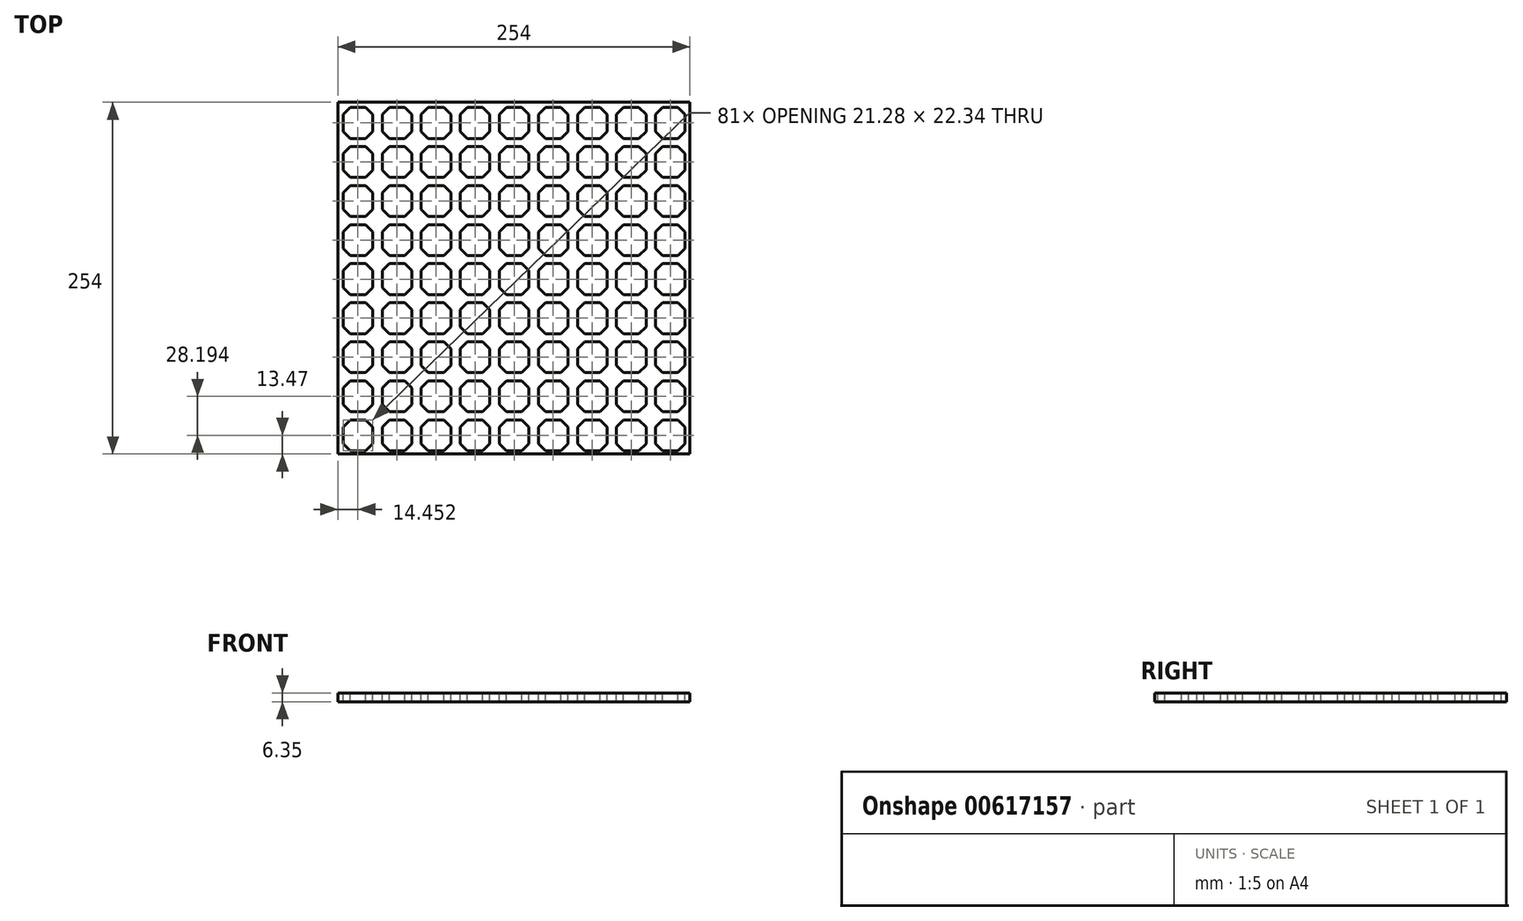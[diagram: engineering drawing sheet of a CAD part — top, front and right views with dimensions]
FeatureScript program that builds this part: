
annotation { "Feature Type Name" : "Feature", "Feature Type Description" : "" }
export const myFeature = defineFeature(function(context is Context, id is Id, definition is map)
    precondition{}
    {
        {
            var Q0;
            Q0=qCreatedBy(makeId("Top.planeOp"),FACE);
            var sketch = newSketch(context, id + "F0", { "sketchPlane" : qUnion([Q0])});
            skLineSegment(sketch, "E0.bottom", {"start": v(-127, 127) * mm, "end": v(127, 127) * mm});
            skLineSegment(sketch, "E0.top", {"start": v(-127, -127) * mm, "end": v(127, -127) * mm});
            skLineSegment(sketch, "E0.left", {"start": v(-127, 127) * mm, "end": v(-127, -127) * mm});
            skLineSegment(sketch, "E0.right", {"start": v(127, 127) * mm, "end": v(127, -127) * mm});
            skSolve(sketch);
        }
        {
            var Q0;
            Q0 = qSketchRegion(id + "F0", true);
            extrude(context, id + "F1", {"entities" : qUnion([Q0]), "depth" : 6.35 * mm, "offsetDistance" : 25.4 * mm});
        }
        {
            var Q0;
            Q0=makeQuery(id+"F1.opExtrude","CAP_FACE",FACE,{"disambiguationData":[OSD([sQuery(id+"F0.wireOp",EDGE,"E0.bottom"),sQuery(id+"F0.wireOp",EDGE,"E0.top"),sQuery(id+"F0.wireOp",EDGE,"E0.left"),sQuery(id+"F0.wireOp",EDGE,"E0.right")])],"isStart":false});
            var sketch = newSketch(context, id + "F2", { "sketchPlane" : qUnion([Q0])});
            skLineSegment(sketch, "E1.bottom", {"start": v(-118.11, 123.2) * mm, "end": v(-106.99, 123.2) * mm});
            skLineSegment(sketch, "E1.top", {"start": v(-118.11, 100.85) * mm, "end": v(-106.99, 100.85) * mm});
            skLineSegment(sketch, "E1.left", {"start": v(-123.2, 118.11) * mm, "end": v(-123.2, 105.93) * mm});
            skLineSegment(sketch, "E1.right", {"start": v(-101.9, 118.11) * mm, "end": v(-101.9, 105.93) * mm});
            skLineSegment(sketch, "E2", {"start": v(-123.2, 118.11) * mm, "end": v(-118.11, 123.2) * mm});
            skPoint(sketch, "E3.orphan", {"position": v(-123.2, 123.2) * mm});
            skLineSegment(sketch, "E4", {"start": v(-106.99, 123.2) * mm, "end": v(-101.9, 118.11) * mm});
            skLineSegment(sketch, "E5", {"start": v(-123.2, 105.93) * mm, "end": v(-118.11, 100.85) * mm});
            skLineSegment(sketch, "E6", {"start": v(-101.9, 105.93) * mm, "end": v(-106.99, 100.85) * mm});
            skPoint(sketch, "E7.orphan", {"position": v(-101.9, 123.2) * mm});
            skPoint(sketch, "E8.orphan", {"position": v(-101.9, 100.85) * mm});
            skPoint(sketch, "E9.orphan", {"position": v(-123.2, 100.85) * mm});
            skLineSegment(sketch, "E10.1.0.0", {"start": v(-73.71, 118.11) * mm, "end": v(-73.71, 105.93) * mm});
            skLineSegment(sketch, "E10.1.0.1", {"start": v(-95, 118.11) * mm, "end": v(-95, 105.93) * mm});
            skLineSegment(sketch, "E10.1.0.2", {"start": v(-89.92, 100.85) * mm, "end": v(-78.8, 100.85) * mm});
            skLineSegment(sketch, "E10.1.0.3", {"start": v(-89.92, 123.2) * mm, "end": v(-78.8, 123.2) * mm});
            skPoint(sketch, "E10.1.0.4", {"position": v(-95, 123.2) * mm});
            skPoint(sketch, "E10.1.0.5", {"position": v(-73.71, 100.85) * mm});
            skPoint(sketch, "E10.1.0.6", {"position": v(-73.71, 123.2) * mm});
            skPoint(sketch, "E10.1.0.7", {"position": v(-95, 100.85) * mm});
            skLineSegment(sketch, "E10.1.0.8", {"start": v(-95, 118.11) * mm, "end": v(-89.92, 123.2) * mm});
            skLineSegment(sketch, "E10.1.0.9", {"start": v(-95, 105.93) * mm, "end": v(-89.92, 100.85) * mm});
            skLineSegment(sketch, "E10.1.0.10", {"start": v(-78.8, 123.2) * mm, "end": v(-73.71, 118.11) * mm});
            skLineSegment(sketch, "E10.1.0.11", {"start": v(-73.71, 105.93) * mm, "end": v(-78.8, 100.85) * mm});
            skLineSegment(sketch, "E10.2.0.0", {"start": v(-45.52, 118.11) * mm, "end": v(-45.52, 105.93) * mm});
            skLineSegment(sketch, "E10.2.0.1", {"start": v(-66.8, 118.11) * mm, "end": v(-66.8, 105.93) * mm});
            skLineSegment(sketch, "E10.2.0.2", {"start": v(-61.72, 100.85) * mm, "end": v(-50.6, 100.85) * mm});
            skLineSegment(sketch, "E10.2.0.3", {"start": v(-61.72, 123.2) * mm, "end": v(-50.6, 123.2) * mm});
            skPoint(sketch, "E10.2.0.4", {"position": v(-66.8, 123.2) * mm});
            skPoint(sketch, "E10.2.0.5", {"position": v(-45.52, 100.85) * mm});
            skPoint(sketch, "E10.2.0.6", {"position": v(-45.52, 123.2) * mm});
            skPoint(sketch, "E10.2.0.7", {"position": v(-66.8, 100.85) * mm});
            skLineSegment(sketch, "E10.2.0.8", {"start": v(-66.8, 118.11) * mm, "end": v(-61.72, 123.2) * mm});
            skLineSegment(sketch, "E10.2.0.9", {"start": v(-66.8, 105.93) * mm, "end": v(-61.72, 100.85) * mm});
            skLineSegment(sketch, "E10.2.0.10", {"start": v(-50.6, 123.2) * mm, "end": v(-45.52, 118.11) * mm});
            skLineSegment(sketch, "E10.2.0.11", {"start": v(-45.52, 105.93) * mm, "end": v(-50.6, 100.85) * mm});
            skLineSegment(sketch, "E10.3.0.0", {"start": v(-17.32, 118.11) * mm, "end": v(-17.32, 105.93) * mm});
            skLineSegment(sketch, "E10.3.0.1", {"start": v(-38.6, 118.11) * mm, "end": v(-38.6, 105.93) * mm});
            skLineSegment(sketch, "E10.3.0.2", {"start": v(-33.53, 100.85) * mm, "end": v(-22.4, 100.85) * mm});
            skLineSegment(sketch, "E10.3.0.3", {"start": v(-33.53, 123.2) * mm, "end": v(-22.4, 123.2) * mm});
            skPoint(sketch, "E10.3.0.4", {"position": v(-38.6, 123.2) * mm});
            skPoint(sketch, "E10.3.0.5", {"position": v(-17.32, 100.85) * mm});
            skPoint(sketch, "E10.3.0.6", {"position": v(-17.32, 123.2) * mm});
            skPoint(sketch, "E10.3.0.7", {"position": v(-38.6, 100.85) * mm});
            skLineSegment(sketch, "E10.3.0.8", {"start": v(-38.6, 118.11) * mm, "end": v(-33.53, 123.2) * mm});
            skLineSegment(sketch, "E10.3.0.9", {"start": v(-38.6, 105.93) * mm, "end": v(-33.53, 100.85) * mm});
            skLineSegment(sketch, "E10.3.0.10", {"start": v(-22.4, 123.2) * mm, "end": v(-17.32, 118.11) * mm});
            skLineSegment(sketch, "E10.3.0.11", {"start": v(-17.32, 105.93) * mm, "end": v(-22.4, 100.85) * mm});
            skLineSegment(sketch, "E10.4.0.0", {"start": v(10.87, 118.11) * mm, "end": v(10.87, 105.93) * mm});
            skLineSegment(sketch, "E10.4.0.1", {"start": v(-10.41, 118.11) * mm, "end": v(-10.41, 105.93) * mm});
            skLineSegment(sketch, "E10.4.0.2", {"start": v(-5.33, 100.85) * mm, "end": v(5.79, 100.85) * mm});
            skLineSegment(sketch, "E10.4.0.3", {"start": v(-5.33, 123.2) * mm, "end": v(5.79, 123.2) * mm});
            skPoint(sketch, "E10.4.0.4", {"position": v(-10.41, 123.2) * mm});
            skPoint(sketch, "E10.4.0.5", {"position": v(10.87, 100.85) * mm});
            skPoint(sketch, "E10.4.0.6", {"position": v(10.87, 123.2) * mm});
            skPoint(sketch, "E10.4.0.7", {"position": v(-10.41, 100.85) * mm});
            skLineSegment(sketch, "E10.4.0.8", {"start": v(-10.41, 118.11) * mm, "end": v(-5.33, 123.2) * mm});
            skLineSegment(sketch, "E10.4.0.9", {"start": v(-10.41, 105.93) * mm, "end": v(-5.33, 100.85) * mm});
            skLineSegment(sketch, "E10.4.0.10", {"start": v(5.79, 123.2) * mm, "end": v(10.87, 118.11) * mm});
            skLineSegment(sketch, "E10.4.0.11", {"start": v(10.87, 105.93) * mm, "end": v(5.79, 100.85) * mm});
            skLineSegment(sketch, "E10.5.0.0", {"start": v(39.06, 118.11) * mm, "end": v(39.06, 105.93) * mm});
            skLineSegment(sketch, "E10.5.0.1", {"start": v(17.78, 118.11) * mm, "end": v(17.78, 105.93) * mm});
            skLineSegment(sketch, "E10.5.0.2", {"start": v(22.86, 100.85) * mm, "end": v(33.98, 100.85) * mm});
            skLineSegment(sketch, "E10.5.0.3", {"start": v(22.86, 123.2) * mm, "end": v(33.98, 123.2) * mm});
            skPoint(sketch, "E10.5.0.4", {"position": v(17.78, 123.2) * mm});
            skPoint(sketch, "E10.5.0.5", {"position": v(39.06, 100.85) * mm});
            skPoint(sketch, "E10.5.0.6", {"position": v(39.06, 123.2) * mm});
            skPoint(sketch, "E10.5.0.7", {"position": v(17.78, 100.85) * mm});
            skLineSegment(sketch, "E10.5.0.8", {"start": v(17.78, 118.11) * mm, "end": v(22.86, 123.2) * mm});
            skLineSegment(sketch, "E10.5.0.9", {"start": v(17.78, 105.93) * mm, "end": v(22.86, 100.85) * mm});
            skLineSegment(sketch, "E10.5.0.10", {"start": v(33.98, 123.2) * mm, "end": v(39.06, 118.11) * mm});
            skLineSegment(sketch, "E10.5.0.11", {"start": v(39.06, 105.93) * mm, "end": v(33.98, 100.85) * mm});
            skLineSegment(sketch, "E10.6.0.0", {"start": v(67.26, 118.11) * mm, "end": v(67.26, 105.93) * mm});
            skLineSegment(sketch, "E10.6.0.1", {"start": v(45.97, 118.11) * mm, "end": v(45.97, 105.93) * mm});
            skLineSegment(sketch, "E10.6.0.2", {"start": v(51.05, 100.85) * mm, "end": v(62.18, 100.85) * mm});
            skLineSegment(sketch, "E10.6.0.3", {"start": v(51.05, 123.2) * mm, "end": v(62.18, 123.2) * mm});
            skPoint(sketch, "E10.6.0.4", {"position": v(45.97, 123.2) * mm});
            skPoint(sketch, "E10.6.0.5", {"position": v(67.26, 100.85) * mm});
            skPoint(sketch, "E10.6.0.6", {"position": v(67.26, 123.2) * mm});
            skPoint(sketch, "E10.6.0.7", {"position": v(45.97, 100.85) * mm});
            skLineSegment(sketch, "E10.6.0.8", {"start": v(45.97, 118.11) * mm, "end": v(51.05, 123.2) * mm});
            skLineSegment(sketch, "E10.6.0.9", {"start": v(45.97, 105.93) * mm, "end": v(51.05, 100.85) * mm});
            skLineSegment(sketch, "E10.6.0.10", {"start": v(62.18, 123.2) * mm, "end": v(67.26, 118.11) * mm});
            skLineSegment(sketch, "E10.6.0.11", {"start": v(67.26, 105.93) * mm, "end": v(62.18, 100.85) * mm});
            skLineSegment(sketch, "E10.7.0.0", {"start": v(95.45, 118.11) * mm, "end": v(95.45, 105.93) * mm});
            skLineSegment(sketch, "E10.7.0.1", {"start": v(74.17, 118.11) * mm, "end": v(74.17, 105.93) * mm});
            skLineSegment(sketch, "E10.7.0.2", {"start": v(79.25, 100.85) * mm, "end": v(90.37, 100.85) * mm});
            skLineSegment(sketch, "E10.7.0.3", {"start": v(79.25, 123.2) * mm, "end": v(90.37, 123.2) * mm});
            skPoint(sketch, "E10.7.0.4", {"position": v(74.17, 123.2) * mm});
            skPoint(sketch, "E10.7.0.5", {"position": v(95.45, 100.85) * mm});
            skPoint(sketch, "E10.7.0.6", {"position": v(95.45, 123.2) * mm});
            skPoint(sketch, "E10.7.0.7", {"position": v(74.17, 100.85) * mm});
            skLineSegment(sketch, "E10.7.0.8", {"start": v(74.17, 118.11) * mm, "end": v(79.25, 123.2) * mm});
            skLineSegment(sketch, "E10.7.0.9", {"start": v(74.17, 105.93) * mm, "end": v(79.25, 100.85) * mm});
            skLineSegment(sketch, "E10.7.0.10", {"start": v(90.37, 123.2) * mm, "end": v(95.45, 118.11) * mm});
            skLineSegment(sketch, "E10.7.0.11", {"start": v(95.45, 105.93) * mm, "end": v(90.37, 100.85) * mm});
            skLineSegment(sketch, "E10.8.0.0", {"start": v(123.65, 118.11) * mm, "end": v(123.65, 105.93) * mm});
            skLineSegment(sketch, "E10.8.0.1", {"start": v(102.36, 118.11) * mm, "end": v(102.36, 105.93) * mm});
            skLineSegment(sketch, "E10.8.0.2", {"start": v(107.44, 100.85) * mm, "end": v(118.57, 100.85) * mm});
            skLineSegment(sketch, "E10.8.0.3", {"start": v(107.44, 123.2) * mm, "end": v(118.57, 123.2) * mm});
            skPoint(sketch, "E10.8.0.4", {"position": v(102.36, 123.2) * mm});
            skPoint(sketch, "E10.8.0.5", {"position": v(123.65, 100.85) * mm});
            skPoint(sketch, "E10.8.0.6", {"position": v(123.65, 123.2) * mm});
            skPoint(sketch, "E10.8.0.7", {"position": v(102.36, 100.85) * mm});
            skLineSegment(sketch, "E10.8.0.8", {"start": v(102.36, 118.11) * mm, "end": v(107.44, 123.2) * mm});
            skLineSegment(sketch, "E10.8.0.9", {"start": v(102.36, 105.93) * mm, "end": v(107.44, 100.85) * mm});
            skLineSegment(sketch, "E10.8.0.10", {"start": v(118.57, 123.2) * mm, "end": v(123.65, 118.11) * mm});
            skLineSegment(sketch, "E10.8.0.11", {"start": v(123.65, 105.93) * mm, "end": v(118.57, 100.85) * mm});
            skLineSegment(sketch, "E10.9.0.0", {"start": v(151.84, 118.11) * mm, "end": v(151.84, 105.93) * mm});
            skLineSegment(sketch, "E10.9.0.1", {"start": v(130.56, 118.11) * mm, "end": v(130.56, 105.93) * mm});
            skLineSegment(sketch, "E10.9.0.2", {"start": v(135.64, 100.85) * mm, "end": v(146.76, 100.85) * mm});
            skLineSegment(sketch, "E10.9.0.3", {"start": v(135.64, 123.2) * mm, "end": v(146.76, 123.2) * mm});
            skPoint(sketch, "E10.9.0.4", {"position": v(130.56, 123.2) * mm});
            skPoint(sketch, "E10.9.0.5", {"position": v(151.84, 100.85) * mm});
            skPoint(sketch, "E10.9.0.6", {"position": v(151.84, 123.2) * mm});
            skPoint(sketch, "E10.9.0.7", {"position": v(130.56, 100.85) * mm});
            skLineSegment(sketch, "E10.9.0.8", {"start": v(130.56, 118.11) * mm, "end": v(135.64, 123.2) * mm});
            skLineSegment(sketch, "E10.9.0.9", {"start": v(130.56, 105.93) * mm, "end": v(135.64, 100.85) * mm});
            skLineSegment(sketch, "E10.9.0.10", {"start": v(146.76, 123.2) * mm, "end": v(151.84, 118.11) * mm});
            skLineSegment(sketch, "E10.9.0.11", {"start": v(151.84, 105.93) * mm, "end": v(146.76, 100.85) * mm});
            skLineSegment(sketch, "E10.direction1", {"start": v(-123.2, 100.85) * mm, "end": v(-95, 100.85) * mm, "construction": true});
            skPoint(sketch, "E11.0.1.0", {"position": v(-73.71, 95) * mm});
            skLineSegment(sketch, "E11.0.1.1", {"start": v(102.36, 89.92) * mm, "end": v(102.36, 77.74) * mm});
            skLineSegment(sketch, "E11.0.1.2", {"start": v(45.97, 89.92) * mm, "end": v(45.97, 77.74) * mm});
            skPoint(sketch, "E11.0.1.3", {"position": v(39.06, 95) * mm});
            skLineSegment(sketch, "E11.0.1.4", {"start": v(-66.8, 89.92) * mm, "end": v(-66.8, 77.74) * mm});
            skLineSegment(sketch, "E11.0.1.5", {"start": v(-95, 89.92) * mm, "end": v(-95, 77.74) * mm});
            skLineSegment(sketch, "E11.0.1.6", {"start": v(-73.71, 89.92) * mm, "end": v(-73.71, 77.74) * mm});
            skLineSegment(sketch, "E11.0.1.7", {"start": v(-123.2, 89.92) * mm, "end": v(-123.2, 77.74) * mm});
            skLineSegment(sketch, "E11.0.1.8", {"start": v(-101.9, 89.92) * mm, "end": v(-101.9, 77.74) * mm});
            skPoint(sketch, "E11.0.1.9", {"position": v(130.56, 72.66) * mm});
            skPoint(sketch, "E11.0.1.10", {"position": v(67.26, 95) * mm});
            skPoint(sketch, "E11.0.1.11", {"position": v(-66.8, 72.66) * mm});
            skPoint(sketch, "E11.0.1.12", {"position": v(10.87, 95) * mm});
            skPoint(sketch, "E11.0.1.13", {"position": v(-101.9, 72.66) * mm});
            skPoint(sketch, "E11.0.1.14", {"position": v(45.97, 72.66) * mm});
            skLineSegment(sketch, "E11.0.1.15", {"start": v(-118.11, 95) * mm, "end": v(-106.99, 95) * mm});
            skPoint(sketch, "E11.0.1.16", {"position": v(-45.52, 95) * mm});
            skPoint(sketch, "E11.0.1.17", {"position": v(151.84, 95) * mm});
            skPoint(sketch, "E11.0.1.18", {"position": v(123.65, 95) * mm});
            skLineSegment(sketch, "E11.0.1.19", {"start": v(151.84, 89.92) * mm, "end": v(151.84, 77.74) * mm});
            skLineSegment(sketch, "E11.0.1.20", {"start": v(95.45, 89.92) * mm, "end": v(95.45, 77.74) * mm});
            skLineSegment(sketch, "E11.0.1.21", {"start": v(39.06, 89.92) * mm, "end": v(39.06, 77.74) * mm});
            skLineSegment(sketch, "E11.0.1.22", {"start": v(-17.32, 89.92) * mm, "end": v(-17.32, 77.74) * mm});
            skPoint(sketch, "E11.0.1.23", {"position": v(74.17, 72.66) * mm});
            skPoint(sketch, "E11.0.1.24", {"position": v(-38.6, 72.66) * mm});
            skLineSegment(sketch, "E11.0.1.25", {"start": v(-10.41, 89.92) * mm, "end": v(-10.41, 77.74) * mm});
            skLineSegment(sketch, "E11.0.1.26", {"start": v(-89.92, 72.66) * mm, "end": v(-78.8, 72.66) * mm});
            skLineSegment(sketch, "E11.0.1.27", {"start": v(-45.52, 89.92) * mm, "end": v(-45.52, 77.74) * mm});
            skLineSegment(sketch, "E11.0.1.28", {"start": v(10.87, 89.92) * mm, "end": v(10.87, 77.74) * mm});
            skPoint(sketch, "E11.0.1.29", {"position": v(-17.32, 95) * mm});
            skPoint(sketch, "E11.0.1.30", {"position": v(95.45, 95) * mm});
            skPoint(sketch, "E11.0.1.31", {"position": v(95.45, 72.66) * mm});
            skPoint(sketch, "E11.0.1.32", {"position": v(151.84, 72.66) * mm});
            skPoint(sketch, "E11.0.1.33", {"position": v(-73.71, 72.66) * mm});
            skPoint(sketch, "E11.0.1.34", {"position": v(39.06, 72.66) * mm});
            skLineSegment(sketch, "E11.0.1.35", {"start": v(67.26, 89.92) * mm, "end": v(67.26, 77.74) * mm});
            skLineSegment(sketch, "E11.0.1.36", {"start": v(123.65, 89.92) * mm, "end": v(123.65, 77.74) * mm});
            skLineSegment(sketch, "E11.0.1.37", {"start": v(-123.2, 72.66) * mm, "end": v(-95, 72.66) * mm, "construction": true});
            skPoint(sketch, "E11.0.1.38", {"position": v(130.56, 95) * mm});
            skPoint(sketch, "E11.0.1.39", {"position": v(45.97, 95) * mm});
            skLineSegment(sketch, "E11.0.1.40", {"start": v(51.05, 95) * mm, "end": v(62.18, 95) * mm});
            skPoint(sketch, "E11.0.1.41", {"position": v(-66.8, 95) * mm});
            skLineSegment(sketch, "E11.0.1.42", {"start": v(107.44, 95) * mm, "end": v(118.57, 95) * mm});
            skLineSegment(sketch, "E11.0.1.43", {"start": v(135.64, 95) * mm, "end": v(146.76, 95) * mm});
            skLineSegment(sketch, "E11.0.1.44", {"start": v(79.25, 95) * mm, "end": v(90.37, 95) * mm});
            skLineSegment(sketch, "E11.0.1.45", {"start": v(22.86, 95) * mm, "end": v(33.98, 95) * mm});
            skLineSegment(sketch, "E11.0.1.46", {"start": v(-33.53, 95) * mm, "end": v(-22.4, 95) * mm});
            skLineSegment(sketch, "E11.0.1.47", {"start": v(-61.72, 95) * mm, "end": v(-50.6, 95) * mm});
            skPoint(sketch, "E11.0.1.48", {"position": v(-17.32, 72.66) * mm});
            skLineSegment(sketch, "E11.0.1.49", {"start": v(-5.33, 95) * mm, "end": v(5.79, 95) * mm});
            skLineSegment(sketch, "E11.0.1.50", {"start": v(-33.53, 72.66) * mm, "end": v(-22.4, 72.66) * mm});
            skLineSegment(sketch, "E11.0.1.51", {"start": v(22.86, 72.66) * mm, "end": v(33.98, 72.66) * mm});
            skPoint(sketch, "E11.0.1.52", {"position": v(17.78, 95) * mm});
            skLineSegment(sketch, "E11.0.1.53", {"start": v(79.25, 72.66) * mm, "end": v(90.37, 72.66) * mm});
            skLineSegment(sketch, "E11.0.1.54", {"start": v(135.64, 72.66) * mm, "end": v(146.76, 72.66) * mm});
            skPoint(sketch, "E11.0.1.55", {"position": v(67.26, 72.66) * mm});
            skPoint(sketch, "E11.0.1.56", {"position": v(-101.9, 95) * mm});
            skPoint(sketch, "E11.0.1.57", {"position": v(10.87, 72.66) * mm});
            skPoint(sketch, "E11.0.1.58", {"position": v(123.65, 72.66) * mm});
            skPoint(sketch, "E11.0.1.59", {"position": v(-45.52, 72.66) * mm});
            skPoint(sketch, "E11.0.1.60", {"position": v(-95, 72.66) * mm});
            skLineSegment(sketch, "E11.0.1.61", {"start": v(51.05, 72.66) * mm, "end": v(62.18, 72.66) * mm});
            skPoint(sketch, "E11.0.1.62", {"position": v(17.78, 72.66) * mm});
            skLineSegment(sketch, "E11.0.1.63", {"start": v(107.44, 72.66) * mm, "end": v(118.57, 72.66) * mm});
            skLineSegment(sketch, "E11.0.1.64", {"start": v(-61.72, 72.66) * mm, "end": v(-50.6, 72.66) * mm});
            skLineSegment(sketch, "E11.0.1.65", {"start": v(-5.33, 72.66) * mm, "end": v(5.79, 72.66) * mm});
            skPoint(sketch, "E11.0.1.66", {"position": v(-123.2, 95) * mm});
            skPoint(sketch, "E11.0.1.67", {"position": v(-10.41, 95) * mm});
            skPoint(sketch, "E11.0.1.68", {"position": v(102.36, 95) * mm});
            skPoint(sketch, "E11.0.1.69", {"position": v(74.17, 95) * mm});
            skPoint(sketch, "E11.0.1.70", {"position": v(-10.41, 72.66) * mm});
            skPoint(sketch, "E11.0.1.71", {"position": v(102.36, 72.66) * mm});
            skPoint(sketch, "E11.0.1.72", {"position": v(-38.6, 95) * mm});
            skPoint(sketch, "E11.0.1.73", {"position": v(-123.2, 72.66) * mm});
            skPoint(sketch, "E11.0.1.74", {"position": v(-95, 95) * mm});
            skLineSegment(sketch, "E11.0.1.75", {"start": v(-38.6, 89.92) * mm, "end": v(-38.6, 77.74) * mm});
            skLineSegment(sketch, "E11.0.1.76", {"start": v(17.78, 89.92) * mm, "end": v(17.78, 77.74) * mm});
            skLineSegment(sketch, "E11.0.1.77", {"start": v(74.17, 89.92) * mm, "end": v(74.17, 77.74) * mm});
            skLineSegment(sketch, "E11.0.1.78", {"start": v(130.56, 89.92) * mm, "end": v(130.56, 77.74) * mm});
            skLineSegment(sketch, "E11.0.1.79", {"start": v(-118.11, 72.66) * mm, "end": v(-106.99, 72.66) * mm});
            skLineSegment(sketch, "E11.0.1.80", {"start": v(-89.92, 95) * mm, "end": v(-78.8, 95) * mm});
            skLineSegment(sketch, "E11.0.1.81", {"start": v(-78.8, 95) * mm, "end": v(-73.71, 89.92) * mm});
            skLineSegment(sketch, "E11.0.1.82", {"start": v(-95, 77.74) * mm, "end": v(-89.92, 72.66) * mm});
            skLineSegment(sketch, "E11.0.1.83", {"start": v(33.98, 95) * mm, "end": v(39.06, 89.92) * mm});
            skLineSegment(sketch, "E11.0.1.84", {"start": v(-73.71, 77.74) * mm, "end": v(-78.8, 72.66) * mm});
            skLineSegment(sketch, "E11.0.1.85", {"start": v(-123.2, 89.92) * mm, "end": v(-118.11, 95) * mm});
            skLineSegment(sketch, "E11.0.1.86", {"start": v(-106.99, 95) * mm, "end": v(-101.9, 89.92) * mm});
            skLineSegment(sketch, "E11.0.1.87", {"start": v(-123.2, 77.74) * mm, "end": v(-118.11, 72.66) * mm});
            skLineSegment(sketch, "E11.0.1.88", {"start": v(-101.9, 77.74) * mm, "end": v(-106.99, 72.66) * mm});
            skLineSegment(sketch, "E11.0.1.89", {"start": v(-45.52, 77.74) * mm, "end": v(-50.6, 72.66) * mm});
            skLineSegment(sketch, "E11.0.1.90", {"start": v(10.87, 77.74) * mm, "end": v(5.79, 72.66) * mm});
            skLineSegment(sketch, "E11.0.1.91", {"start": v(67.26, 77.74) * mm, "end": v(62.18, 72.66) * mm});
            skLineSegment(sketch, "E11.0.1.92", {"start": v(123.65, 77.74) * mm, "end": v(118.57, 72.66) * mm});
            skLineSegment(sketch, "E11.0.1.93", {"start": v(62.18, 95) * mm, "end": v(67.26, 89.92) * mm});
            skLineSegment(sketch, "E11.0.1.94", {"start": v(39.06, 77.74) * mm, "end": v(33.98, 72.66) * mm});
            skLineSegment(sketch, "E11.0.1.95", {"start": v(118.57, 95) * mm, "end": v(123.65, 89.92) * mm});
            skLineSegment(sketch, "E11.0.1.96", {"start": v(95.45, 77.74) * mm, "end": v(90.37, 72.66) * mm});
            skLineSegment(sketch, "E11.0.1.97", {"start": v(151.84, 77.74) * mm, "end": v(146.76, 72.66) * mm});
            skLineSegment(sketch, "E11.0.1.98", {"start": v(-50.6, 95) * mm, "end": v(-45.52, 89.92) * mm});
            skLineSegment(sketch, "E11.0.1.99", {"start": v(5.79, 95) * mm, "end": v(10.87, 89.92) * mm});
            skLineSegment(sketch, "E11.0.1.100", {"start": v(-17.32, 77.74) * mm, "end": v(-22.4, 72.66) * mm});
            skLineSegment(sketch, "E11.0.1.101", {"start": v(-38.6, 77.74) * mm, "end": v(-33.53, 72.66) * mm});
            skLineSegment(sketch, "E11.0.1.102", {"start": v(-10.41, 89.92) * mm, "end": v(-5.33, 95) * mm});
            skLineSegment(sketch, "E11.0.1.103", {"start": v(-66.8, 89.92) * mm, "end": v(-61.72, 95) * mm});
            skLineSegment(sketch, "E11.0.1.104", {"start": v(130.56, 77.74) * mm, "end": v(135.64, 72.66) * mm});
            skLineSegment(sketch, "E11.0.1.105", {"start": v(102.36, 89.92) * mm, "end": v(107.44, 95) * mm});
            skLineSegment(sketch, "E11.0.1.106", {"start": v(74.17, 77.74) * mm, "end": v(79.25, 72.66) * mm});
            skLineSegment(sketch, "E11.0.1.107", {"start": v(45.97, 89.92) * mm, "end": v(51.05, 95) * mm});
            skLineSegment(sketch, "E11.0.1.108", {"start": v(17.78, 77.74) * mm, "end": v(22.86, 72.66) * mm});
            skLineSegment(sketch, "E11.0.1.109", {"start": v(130.56, 89.92) * mm, "end": v(135.64, 95) * mm});
            skLineSegment(sketch, "E11.0.1.110", {"start": v(74.17, 89.92) * mm, "end": v(79.25, 95) * mm});
            skLineSegment(sketch, "E11.0.1.111", {"start": v(17.78, 89.92) * mm, "end": v(22.86, 95) * mm});
            skLineSegment(sketch, "E11.0.1.112", {"start": v(-95, 89.92) * mm, "end": v(-89.92, 95) * mm});
            skLineSegment(sketch, "E11.0.1.113", {"start": v(-38.6, 89.92) * mm, "end": v(-33.53, 95) * mm});
            skLineSegment(sketch, "E11.0.1.114", {"start": v(-22.4, 95) * mm, "end": v(-17.32, 89.92) * mm});
            skLineSegment(sketch, "E11.0.1.115", {"start": v(-10.41, 77.74) * mm, "end": v(-5.33, 72.66) * mm});
            skLineSegment(sketch, "E11.0.1.116", {"start": v(-66.8, 77.74) * mm, "end": v(-61.72, 72.66) * mm});
            skLineSegment(sketch, "E11.0.1.117", {"start": v(146.76, 95) * mm, "end": v(151.84, 89.92) * mm});
            skLineSegment(sketch, "E11.0.1.118", {"start": v(102.36, 77.74) * mm, "end": v(107.44, 72.66) * mm});
            skLineSegment(sketch, "E11.0.1.119", {"start": v(90.37, 95) * mm, "end": v(95.45, 89.92) * mm});
            skLineSegment(sketch, "E11.0.1.120", {"start": v(45.97, 77.74) * mm, "end": v(51.05, 72.66) * mm});
            skPoint(sketch, "E11.0.2.0", {"position": v(-73.71, 66.8) * mm});
            skLineSegment(sketch, "E11.0.2.1", {"start": v(102.36, 61.72) * mm, "end": v(102.36, 49.55) * mm});
            skLineSegment(sketch, "E11.0.2.2", {"start": v(45.97, 61.72) * mm, "end": v(45.97, 49.55) * mm});
            skPoint(sketch, "E11.0.2.3", {"position": v(39.06, 66.8) * mm});
            skLineSegment(sketch, "E11.0.2.4", {"start": v(-66.8, 61.72) * mm, "end": v(-66.8, 49.55) * mm});
            skLineSegment(sketch, "E11.0.2.5", {"start": v(-95, 61.72) * mm, "end": v(-95, 49.55) * mm});
            skLineSegment(sketch, "E11.0.2.6", {"start": v(-73.71, 61.72) * mm, "end": v(-73.71, 49.55) * mm});
            skLineSegment(sketch, "E11.0.2.7", {"start": v(-123.2, 61.72) * mm, "end": v(-123.2, 49.55) * mm});
            skLineSegment(sketch, "E11.0.2.8", {"start": v(-101.9, 61.72) * mm, "end": v(-101.9, 49.55) * mm});
            skPoint(sketch, "E11.0.2.9", {"position": v(130.56, 44.47) * mm});
            skPoint(sketch, "E11.0.2.10", {"position": v(67.26, 66.8) * mm});
            skPoint(sketch, "E11.0.2.11", {"position": v(-66.8, 44.47) * mm});
            skPoint(sketch, "E11.0.2.12", {"position": v(10.87, 66.8) * mm});
            skPoint(sketch, "E11.0.2.13", {"position": v(-101.9, 44.47) * mm});
            skPoint(sketch, "E11.0.2.14", {"position": v(45.97, 44.47) * mm});
            skLineSegment(sketch, "E11.0.2.15", {"start": v(-118.11, 66.8) * mm, "end": v(-106.99, 66.8) * mm});
            skPoint(sketch, "E11.0.2.16", {"position": v(-45.52, 66.8) * mm});
            skPoint(sketch, "E11.0.2.17", {"position": v(151.84, 66.8) * mm});
            skPoint(sketch, "E11.0.2.18", {"position": v(123.65, 66.8) * mm});
            skLineSegment(sketch, "E11.0.2.19", {"start": v(151.84, 61.72) * mm, "end": v(151.84, 49.55) * mm});
            skLineSegment(sketch, "E11.0.2.20", {"start": v(95.45, 61.72) * mm, "end": v(95.45, 49.55) * mm});
            skLineSegment(sketch, "E11.0.2.21", {"start": v(39.06, 61.72) * mm, "end": v(39.06, 49.55) * mm});
            skLineSegment(sketch, "E11.0.2.22", {"start": v(-17.32, 61.72) * mm, "end": v(-17.32, 49.55) * mm});
            skPoint(sketch, "E11.0.2.23", {"position": v(74.17, 44.47) * mm});
            skPoint(sketch, "E11.0.2.24", {"position": v(-38.6, 44.47) * mm});
            skLineSegment(sketch, "E11.0.2.25", {"start": v(-10.41, 61.72) * mm, "end": v(-10.41, 49.55) * mm});
            skLineSegment(sketch, "E11.0.2.26", {"start": v(-89.92, 44.47) * mm, "end": v(-78.8, 44.47) * mm});
            skLineSegment(sketch, "E11.0.2.27", {"start": v(-45.52, 61.72) * mm, "end": v(-45.52, 49.55) * mm});
            skLineSegment(sketch, "E11.0.2.28", {"start": v(10.87, 61.72) * mm, "end": v(10.87, 49.55) * mm});
            skPoint(sketch, "E11.0.2.29", {"position": v(-17.32, 66.8) * mm});
            skPoint(sketch, "E11.0.2.30", {"position": v(95.45, 66.8) * mm});
            skPoint(sketch, "E11.0.2.31", {"position": v(95.45, 44.47) * mm});
            skPoint(sketch, "E11.0.2.32", {"position": v(151.84, 44.47) * mm});
            skPoint(sketch, "E11.0.2.33", {"position": v(-73.71, 44.47) * mm});
            skPoint(sketch, "E11.0.2.34", {"position": v(39.06, 44.47) * mm});
            skLineSegment(sketch, "E11.0.2.35", {"start": v(67.26, 61.72) * mm, "end": v(67.26, 49.55) * mm});
            skLineSegment(sketch, "E11.0.2.36", {"start": v(123.65, 61.72) * mm, "end": v(123.65, 49.55) * mm});
            skLineSegment(sketch, "E11.0.2.37", {"start": v(-123.2, 44.47) * mm, "end": v(-95, 44.47) * mm, "construction": true});
            skPoint(sketch, "E11.0.2.38", {"position": v(130.56, 66.8) * mm});
            skPoint(sketch, "E11.0.2.39", {"position": v(45.97, 66.8) * mm});
            skLineSegment(sketch, "E11.0.2.40", {"start": v(51.05, 66.8) * mm, "end": v(62.18, 66.8) * mm});
            skPoint(sketch, "E11.0.2.41", {"position": v(-66.8, 66.8) * mm});
            skLineSegment(sketch, "E11.0.2.42", {"start": v(107.44, 66.8) * mm, "end": v(118.57, 66.8) * mm});
            skLineSegment(sketch, "E11.0.2.43", {"start": v(135.64, 66.8) * mm, "end": v(146.76, 66.8) * mm});
            skLineSegment(sketch, "E11.0.2.44", {"start": v(79.25, 66.8) * mm, "end": v(90.37, 66.8) * mm});
            skLineSegment(sketch, "E11.0.2.45", {"start": v(22.86, 66.8) * mm, "end": v(33.98, 66.8) * mm});
            skLineSegment(sketch, "E11.0.2.46", {"start": v(-33.53, 66.8) * mm, "end": v(-22.4, 66.8) * mm});
            skLineSegment(sketch, "E11.0.2.47", {"start": v(-61.72, 66.8) * mm, "end": v(-50.6, 66.8) * mm});
            skPoint(sketch, "E11.0.2.48", {"position": v(-17.32, 44.47) * mm});
            skLineSegment(sketch, "E11.0.2.49", {"start": v(-5.33, 66.8) * mm, "end": v(5.79, 66.8) * mm});
            skLineSegment(sketch, "E11.0.2.50", {"start": v(-33.53, 44.47) * mm, "end": v(-22.4, 44.47) * mm});
            skLineSegment(sketch, "E11.0.2.51", {"start": v(22.86, 44.47) * mm, "end": v(33.98, 44.47) * mm});
            skPoint(sketch, "E11.0.2.52", {"position": v(17.78, 66.8) * mm});
            skLineSegment(sketch, "E11.0.2.53", {"start": v(79.25, 44.47) * mm, "end": v(90.37, 44.47) * mm});
            skLineSegment(sketch, "E11.0.2.54", {"start": v(135.64, 44.47) * mm, "end": v(146.76, 44.47) * mm});
            skPoint(sketch, "E11.0.2.55", {"position": v(67.26, 44.47) * mm});
            skPoint(sketch, "E11.0.2.56", {"position": v(-101.9, 66.8) * mm});
            skPoint(sketch, "E11.0.2.57", {"position": v(10.87, 44.47) * mm});
            skPoint(sketch, "E11.0.2.58", {"position": v(123.65, 44.47) * mm});
            skPoint(sketch, "E11.0.2.59", {"position": v(-45.52, 44.47) * mm});
            skPoint(sketch, "E11.0.2.60", {"position": v(-95, 44.47) * mm});
            skLineSegment(sketch, "E11.0.2.61", {"start": v(51.05, 44.47) * mm, "end": v(62.18, 44.47) * mm});
            skPoint(sketch, "E11.0.2.62", {"position": v(17.78, 44.47) * mm});
            skLineSegment(sketch, "E11.0.2.63", {"start": v(107.44, 44.47) * mm, "end": v(118.57, 44.47) * mm});
            skLineSegment(sketch, "E11.0.2.64", {"start": v(-61.72, 44.47) * mm, "end": v(-50.6, 44.47) * mm});
            skLineSegment(sketch, "E11.0.2.65", {"start": v(-5.33, 44.47) * mm, "end": v(5.79, 44.47) * mm});
            skPoint(sketch, "E11.0.2.66", {"position": v(-123.2, 66.8) * mm});
            skPoint(sketch, "E11.0.2.67", {"position": v(-10.41, 66.8) * mm});
            skPoint(sketch, "E11.0.2.68", {"position": v(102.36, 66.8) * mm});
            skPoint(sketch, "E11.0.2.69", {"position": v(74.17, 66.8) * mm});
            skPoint(sketch, "E11.0.2.70", {"position": v(-10.41, 44.47) * mm});
            skPoint(sketch, "E11.0.2.71", {"position": v(102.36, 44.47) * mm});
            skPoint(sketch, "E11.0.2.72", {"position": v(-38.6, 66.8) * mm});
            skPoint(sketch, "E11.0.2.73", {"position": v(-123.2, 44.47) * mm});
            skPoint(sketch, "E11.0.2.74", {"position": v(-95, 66.8) * mm});
            skLineSegment(sketch, "E11.0.2.75", {"start": v(-38.6, 61.72) * mm, "end": v(-38.6, 49.55) * mm});
            skLineSegment(sketch, "E11.0.2.76", {"start": v(17.78, 61.72) * mm, "end": v(17.78, 49.55) * mm});
            skLineSegment(sketch, "E11.0.2.77", {"start": v(74.17, 61.72) * mm, "end": v(74.17, 49.55) * mm});
            skLineSegment(sketch, "E11.0.2.78", {"start": v(130.56, 61.72) * mm, "end": v(130.56, 49.55) * mm});
            skLineSegment(sketch, "E11.0.2.79", {"start": v(-118.11, 44.47) * mm, "end": v(-106.99, 44.47) * mm});
            skLineSegment(sketch, "E11.0.2.80", {"start": v(-89.92, 66.8) * mm, "end": v(-78.8, 66.8) * mm});
            skLineSegment(sketch, "E11.0.2.81", {"start": v(-78.8, 66.8) * mm, "end": v(-73.71, 61.72) * mm});
            skLineSegment(sketch, "E11.0.2.82", {"start": v(-95, 49.55) * mm, "end": v(-89.92, 44.47) * mm});
            skLineSegment(sketch, "E11.0.2.83", {"start": v(33.98, 66.8) * mm, "end": v(39.06, 61.72) * mm});
            skLineSegment(sketch, "E11.0.2.84", {"start": v(-73.71, 49.55) * mm, "end": v(-78.8, 44.47) * mm});
            skLineSegment(sketch, "E11.0.2.85", {"start": v(-123.2, 61.72) * mm, "end": v(-118.11, 66.8) * mm});
            skLineSegment(sketch, "E11.0.2.86", {"start": v(-106.99, 66.8) * mm, "end": v(-101.9, 61.72) * mm});
            skLineSegment(sketch, "E11.0.2.87", {"start": v(-123.2, 49.55) * mm, "end": v(-118.11, 44.47) * mm});
            skLineSegment(sketch, "E11.0.2.88", {"start": v(-101.9, 49.55) * mm, "end": v(-106.99, 44.47) * mm});
            skLineSegment(sketch, "E11.0.2.89", {"start": v(-45.52, 49.55) * mm, "end": v(-50.6, 44.47) * mm});
            skLineSegment(sketch, "E11.0.2.90", {"start": v(10.87, 49.55) * mm, "end": v(5.79, 44.47) * mm});
            skLineSegment(sketch, "E11.0.2.91", {"start": v(67.26, 49.55) * mm, "end": v(62.18, 44.47) * mm});
            skLineSegment(sketch, "E11.0.2.92", {"start": v(123.65, 49.55) * mm, "end": v(118.57, 44.47) * mm});
            skLineSegment(sketch, "E11.0.2.93", {"start": v(62.18, 66.8) * mm, "end": v(67.26, 61.72) * mm});
            skLineSegment(sketch, "E11.0.2.94", {"start": v(39.06, 49.55) * mm, "end": v(33.98, 44.47) * mm});
            skLineSegment(sketch, "E11.0.2.95", {"start": v(118.57, 66.8) * mm, "end": v(123.65, 61.72) * mm});
            skLineSegment(sketch, "E11.0.2.96", {"start": v(95.45, 49.55) * mm, "end": v(90.37, 44.47) * mm});
            skLineSegment(sketch, "E11.0.2.97", {"start": v(151.84, 49.55) * mm, "end": v(146.76, 44.47) * mm});
            skLineSegment(sketch, "E11.0.2.98", {"start": v(-50.6, 66.8) * mm, "end": v(-45.52, 61.72) * mm});
            skLineSegment(sketch, "E11.0.2.99", {"start": v(5.79, 66.8) * mm, "end": v(10.87, 61.72) * mm});
            skLineSegment(sketch, "E11.0.2.100", {"start": v(-17.32, 49.55) * mm, "end": v(-22.4, 44.47) * mm});
            skLineSegment(sketch, "E11.0.2.101", {"start": v(-38.6, 49.55) * mm, "end": v(-33.53, 44.47) * mm});
            skLineSegment(sketch, "E11.0.2.102", {"start": v(-10.41, 61.72) * mm, "end": v(-5.33, 66.8) * mm});
            skLineSegment(sketch, "E11.0.2.103", {"start": v(-66.8, 61.72) * mm, "end": v(-61.72, 66.8) * mm});
            skLineSegment(sketch, "E11.0.2.104", {"start": v(130.56, 49.55) * mm, "end": v(135.64, 44.47) * mm});
            skLineSegment(sketch, "E11.0.2.105", {"start": v(102.36, 61.72) * mm, "end": v(107.44, 66.8) * mm});
            skLineSegment(sketch, "E11.0.2.106", {"start": v(74.17, 49.55) * mm, "end": v(79.25, 44.47) * mm});
            skLineSegment(sketch, "E11.0.2.107", {"start": v(45.97, 61.72) * mm, "end": v(51.05, 66.8) * mm});
            skLineSegment(sketch, "E11.0.2.108", {"start": v(17.78, 49.55) * mm, "end": v(22.86, 44.47) * mm});
            skLineSegment(sketch, "E11.0.2.109", {"start": v(130.56, 61.72) * mm, "end": v(135.64, 66.8) * mm});
            skLineSegment(sketch, "E11.0.2.110", {"start": v(74.17, 61.72) * mm, "end": v(79.25, 66.8) * mm});
            skLineSegment(sketch, "E11.0.2.111", {"start": v(17.78, 61.72) * mm, "end": v(22.86, 66.8) * mm});
            skLineSegment(sketch, "E11.0.2.112", {"start": v(-95, 61.72) * mm, "end": v(-89.92, 66.8) * mm});
            skLineSegment(sketch, "E11.0.2.113", {"start": v(-38.6, 61.72) * mm, "end": v(-33.53, 66.8) * mm});
            skLineSegment(sketch, "E11.0.2.114", {"start": v(-22.4, 66.8) * mm, "end": v(-17.32, 61.72) * mm});
            skLineSegment(sketch, "E11.0.2.115", {"start": v(-10.41, 49.55) * mm, "end": v(-5.33, 44.47) * mm});
            skLineSegment(sketch, "E11.0.2.116", {"start": v(-66.8, 49.55) * mm, "end": v(-61.72, 44.47) * mm});
            skLineSegment(sketch, "E11.0.2.117", {"start": v(146.76, 66.8) * mm, "end": v(151.84, 61.72) * mm});
            skLineSegment(sketch, "E11.0.2.118", {"start": v(102.36, 49.55) * mm, "end": v(107.44, 44.47) * mm});
            skLineSegment(sketch, "E11.0.2.119", {"start": v(90.37, 66.8) * mm, "end": v(95.45, 61.72) * mm});
            skLineSegment(sketch, "E11.0.2.120", {"start": v(45.97, 49.55) * mm, "end": v(51.05, 44.47) * mm});
            skPoint(sketch, "E11.0.3.0", {"position": v(-73.71, 38.6) * mm});
            skLineSegment(sketch, "E11.0.3.1", {"start": v(102.36, 33.53) * mm, "end": v(102.36, 21.35) * mm});
            skLineSegment(sketch, "E11.0.3.2", {"start": v(45.97, 33.53) * mm, "end": v(45.97, 21.35) * mm});
            skPoint(sketch, "E11.0.3.3", {"position": v(39.06, 38.6) * mm});
            skLineSegment(sketch, "E11.0.3.4", {"start": v(-66.8, 33.53) * mm, "end": v(-66.8, 21.35) * mm});
            skLineSegment(sketch, "E11.0.3.5", {"start": v(-95, 33.53) * mm, "end": v(-95, 21.35) * mm});
            skLineSegment(sketch, "E11.0.3.6", {"start": v(-73.71, 33.53) * mm, "end": v(-73.71, 21.35) * mm});
            skLineSegment(sketch, "E11.0.3.7", {"start": v(-123.2, 33.53) * mm, "end": v(-123.2, 21.35) * mm});
            skLineSegment(sketch, "E11.0.3.8", {"start": v(-101.9, 33.53) * mm, "end": v(-101.9, 21.35) * mm});
            skPoint(sketch, "E11.0.3.9", {"position": v(130.56, 16.27) * mm});
            skPoint(sketch, "E11.0.3.10", {"position": v(67.26, 38.6) * mm});
            skPoint(sketch, "E11.0.3.11", {"position": v(-66.8, 16.27) * mm});
            skPoint(sketch, "E11.0.3.12", {"position": v(10.87, 38.6) * mm});
            skPoint(sketch, "E11.0.3.13", {"position": v(-101.9, 16.27) * mm});
            skPoint(sketch, "E11.0.3.14", {"position": v(45.97, 16.27) * mm});
            skLineSegment(sketch, "E11.0.3.15", {"start": v(-118.11, 38.6) * mm, "end": v(-106.99, 38.6) * mm});
            skPoint(sketch, "E11.0.3.16", {"position": v(-45.52, 38.6) * mm});
            skPoint(sketch, "E11.0.3.17", {"position": v(151.84, 38.6) * mm});
            skPoint(sketch, "E11.0.3.18", {"position": v(123.65, 38.6) * mm});
            skLineSegment(sketch, "E11.0.3.19", {"start": v(151.84, 33.53) * mm, "end": v(151.84, 21.35) * mm});
            skLineSegment(sketch, "E11.0.3.20", {"start": v(95.45, 33.53) * mm, "end": v(95.45, 21.35) * mm});
            skLineSegment(sketch, "E11.0.3.21", {"start": v(39.06, 33.53) * mm, "end": v(39.06, 21.35) * mm});
            skLineSegment(sketch, "E11.0.3.22", {"start": v(-17.32, 33.53) * mm, "end": v(-17.32, 21.35) * mm});
            skPoint(sketch, "E11.0.3.23", {"position": v(74.17, 16.27) * mm});
            skPoint(sketch, "E11.0.3.24", {"position": v(-38.6, 16.27) * mm});
            skLineSegment(sketch, "E11.0.3.25", {"start": v(-10.41, 33.53) * mm, "end": v(-10.41, 21.35) * mm});
            skLineSegment(sketch, "E11.0.3.26", {"start": v(-89.92, 16.27) * mm, "end": v(-78.8, 16.27) * mm});
            skLineSegment(sketch, "E11.0.3.27", {"start": v(-45.52, 33.53) * mm, "end": v(-45.52, 21.35) * mm});
            skLineSegment(sketch, "E11.0.3.28", {"start": v(10.87, 33.53) * mm, "end": v(10.87, 21.35) * mm});
            skPoint(sketch, "E11.0.3.29", {"position": v(-17.32, 38.6) * mm});
            skPoint(sketch, "E11.0.3.30", {"position": v(95.45, 38.6) * mm});
            skPoint(sketch, "E11.0.3.31", {"position": v(95.45, 16.27) * mm});
            skPoint(sketch, "E11.0.3.32", {"position": v(151.84, 16.27) * mm});
            skPoint(sketch, "E11.0.3.33", {"position": v(-73.71, 16.27) * mm});
            skPoint(sketch, "E11.0.3.34", {"position": v(39.06, 16.27) * mm});
            skLineSegment(sketch, "E11.0.3.35", {"start": v(67.26, 33.53) * mm, "end": v(67.26, 21.35) * mm});
            skLineSegment(sketch, "E11.0.3.36", {"start": v(123.65, 33.53) * mm, "end": v(123.65, 21.35) * mm});
            skLineSegment(sketch, "E11.0.3.37", {"start": v(-123.2, 16.27) * mm, "end": v(-95, 16.27) * mm, "construction": true});
            skPoint(sketch, "E11.0.3.38", {"position": v(130.56, 38.6) * mm});
            skPoint(sketch, "E11.0.3.39", {"position": v(45.97, 38.6) * mm});
            skLineSegment(sketch, "E11.0.3.40", {"start": v(51.05, 38.6) * mm, "end": v(62.18, 38.6) * mm});
            skPoint(sketch, "E11.0.3.41", {"position": v(-66.8, 38.6) * mm});
            skLineSegment(sketch, "E11.0.3.42", {"start": v(107.44, 38.6) * mm, "end": v(118.57, 38.6) * mm});
            skLineSegment(sketch, "E11.0.3.43", {"start": v(135.64, 38.6) * mm, "end": v(146.76, 38.6) * mm});
            skLineSegment(sketch, "E11.0.3.44", {"start": v(79.25, 38.6) * mm, "end": v(90.37, 38.6) * mm});
            skLineSegment(sketch, "E11.0.3.45", {"start": v(22.86, 38.6) * mm, "end": v(33.98, 38.6) * mm});
            skLineSegment(sketch, "E11.0.3.46", {"start": v(-33.53, 38.6) * mm, "end": v(-22.4, 38.6) * mm});
            skLineSegment(sketch, "E11.0.3.47", {"start": v(-61.72, 38.6) * mm, "end": v(-50.6, 38.6) * mm});
            skPoint(sketch, "E11.0.3.48", {"position": v(-17.32, 16.27) * mm});
            skLineSegment(sketch, "E11.0.3.49", {"start": v(-5.33, 38.6) * mm, "end": v(5.79, 38.6) * mm});
            skLineSegment(sketch, "E11.0.3.50", {"start": v(-33.53, 16.27) * mm, "end": v(-22.4, 16.27) * mm});
            skLineSegment(sketch, "E11.0.3.51", {"start": v(22.86, 16.27) * mm, "end": v(33.98, 16.27) * mm});
            skPoint(sketch, "E11.0.3.52", {"position": v(17.78, 38.6) * mm});
            skLineSegment(sketch, "E11.0.3.53", {"start": v(79.25, 16.27) * mm, "end": v(90.37, 16.27) * mm});
            skLineSegment(sketch, "E11.0.3.54", {"start": v(135.64, 16.27) * mm, "end": v(146.76, 16.27) * mm});
            skPoint(sketch, "E11.0.3.55", {"position": v(67.26, 16.27) * mm});
            skPoint(sketch, "E11.0.3.56", {"position": v(-101.9, 38.6) * mm});
            skPoint(sketch, "E11.0.3.57", {"position": v(10.87, 16.27) * mm});
            skPoint(sketch, "E11.0.3.58", {"position": v(123.65, 16.27) * mm});
            skPoint(sketch, "E11.0.3.59", {"position": v(-45.52, 16.27) * mm});
            skPoint(sketch, "E11.0.3.60", {"position": v(-95, 16.27) * mm});
            skLineSegment(sketch, "E11.0.3.61", {"start": v(51.05, 16.27) * mm, "end": v(62.18, 16.27) * mm});
            skPoint(sketch, "E11.0.3.62", {"position": v(17.78, 16.27) * mm});
            skLineSegment(sketch, "E11.0.3.63", {"start": v(107.44, 16.27) * mm, "end": v(118.57, 16.27) * mm});
            skLineSegment(sketch, "E11.0.3.64", {"start": v(-61.72, 16.27) * mm, "end": v(-50.6, 16.27) * mm});
            skLineSegment(sketch, "E11.0.3.65", {"start": v(-5.33, 16.27) * mm, "end": v(5.79, 16.27) * mm});
            skPoint(sketch, "E11.0.3.66", {"position": v(-123.2, 38.6) * mm});
            skPoint(sketch, "E11.0.3.67", {"position": v(-10.41, 38.6) * mm});
            skPoint(sketch, "E11.0.3.68", {"position": v(102.36, 38.6) * mm});
            skPoint(sketch, "E11.0.3.69", {"position": v(74.17, 38.6) * mm});
            skPoint(sketch, "E11.0.3.70", {"position": v(-10.41, 16.27) * mm});
            skPoint(sketch, "E11.0.3.71", {"position": v(102.36, 16.27) * mm});
            skPoint(sketch, "E11.0.3.72", {"position": v(-38.6, 38.6) * mm});
            skPoint(sketch, "E11.0.3.73", {"position": v(-123.2, 16.27) * mm});
            skPoint(sketch, "E11.0.3.74", {"position": v(-95, 38.6) * mm});
            skLineSegment(sketch, "E11.0.3.75", {"start": v(-38.6, 33.53) * mm, "end": v(-38.6, 21.35) * mm});
            skLineSegment(sketch, "E11.0.3.76", {"start": v(17.78, 33.53) * mm, "end": v(17.78, 21.35) * mm});
            skLineSegment(sketch, "E11.0.3.77", {"start": v(74.17, 33.53) * mm, "end": v(74.17, 21.35) * mm});
            skLineSegment(sketch, "E11.0.3.78", {"start": v(130.56, 33.53) * mm, "end": v(130.56, 21.35) * mm});
            skLineSegment(sketch, "E11.0.3.79", {"start": v(-118.11, 16.27) * mm, "end": v(-106.99, 16.27) * mm});
            skLineSegment(sketch, "E11.0.3.80", {"start": v(-89.92, 38.6) * mm, "end": v(-78.8, 38.6) * mm});
            skLineSegment(sketch, "E11.0.3.81", {"start": v(-78.8, 38.6) * mm, "end": v(-73.71, 33.53) * mm});
            skLineSegment(sketch, "E11.0.3.82", {"start": v(-95, 21.35) * mm, "end": v(-89.92, 16.27) * mm});
            skLineSegment(sketch, "E11.0.3.83", {"start": v(33.98, 38.6) * mm, "end": v(39.06, 33.53) * mm});
            skLineSegment(sketch, "E11.0.3.84", {"start": v(-73.71, 21.35) * mm, "end": v(-78.8, 16.27) * mm});
            skLineSegment(sketch, "E11.0.3.85", {"start": v(-123.2, 33.53) * mm, "end": v(-118.11, 38.6) * mm});
            skLineSegment(sketch, "E11.0.3.86", {"start": v(-106.99, 38.6) * mm, "end": v(-101.9, 33.53) * mm});
            skLineSegment(sketch, "E11.0.3.87", {"start": v(-123.2, 21.35) * mm, "end": v(-118.11, 16.27) * mm});
            skLineSegment(sketch, "E11.0.3.88", {"start": v(-101.9, 21.35) * mm, "end": v(-106.99, 16.27) * mm});
            skLineSegment(sketch, "E11.0.3.89", {"start": v(-45.52, 21.35) * mm, "end": v(-50.6, 16.27) * mm});
            skLineSegment(sketch, "E11.0.3.90", {"start": v(10.87, 21.35) * mm, "end": v(5.79, 16.27) * mm});
            skLineSegment(sketch, "E11.0.3.91", {"start": v(67.26, 21.35) * mm, "end": v(62.18, 16.27) * mm});
            skLineSegment(sketch, "E11.0.3.92", {"start": v(123.65, 21.35) * mm, "end": v(118.57, 16.27) * mm});
            skLineSegment(sketch, "E11.0.3.93", {"start": v(62.18, 38.6) * mm, "end": v(67.26, 33.53) * mm});
            skLineSegment(sketch, "E11.0.3.94", {"start": v(39.06, 21.35) * mm, "end": v(33.98, 16.27) * mm});
            skLineSegment(sketch, "E11.0.3.95", {"start": v(118.57, 38.6) * mm, "end": v(123.65, 33.53) * mm});
            skLineSegment(sketch, "E11.0.3.96", {"start": v(95.45, 21.35) * mm, "end": v(90.37, 16.27) * mm});
            skLineSegment(sketch, "E11.0.3.97", {"start": v(151.84, 21.35) * mm, "end": v(146.76, 16.27) * mm});
            skLineSegment(sketch, "E11.0.3.98", {"start": v(-50.6, 38.6) * mm, "end": v(-45.52, 33.53) * mm});
            skLineSegment(sketch, "E11.0.3.99", {"start": v(5.79, 38.6) * mm, "end": v(10.87, 33.53) * mm});
            skLineSegment(sketch, "E11.0.3.100", {"start": v(-17.32, 21.35) * mm, "end": v(-22.4, 16.27) * mm});
            skLineSegment(sketch, "E11.0.3.101", {"start": v(-38.6, 21.35) * mm, "end": v(-33.53, 16.27) * mm});
            skLineSegment(sketch, "E11.0.3.102", {"start": v(-10.41, 33.53) * mm, "end": v(-5.33, 38.6) * mm});
            skLineSegment(sketch, "E11.0.3.103", {"start": v(-66.8, 33.53) * mm, "end": v(-61.72, 38.6) * mm});
            skLineSegment(sketch, "E11.0.3.104", {"start": v(130.56, 21.35) * mm, "end": v(135.64, 16.27) * mm});
            skLineSegment(sketch, "E11.0.3.105", {"start": v(102.36, 33.53) * mm, "end": v(107.44, 38.6) * mm});
            skLineSegment(sketch, "E11.0.3.106", {"start": v(74.17, 21.35) * mm, "end": v(79.25, 16.27) * mm});
            skLineSegment(sketch, "E11.0.3.107", {"start": v(45.97, 33.53) * mm, "end": v(51.05, 38.6) * mm});
            skLineSegment(sketch, "E11.0.3.108", {"start": v(17.78, 21.35) * mm, "end": v(22.86, 16.27) * mm});
            skLineSegment(sketch, "E11.0.3.109", {"start": v(130.56, 33.53) * mm, "end": v(135.64, 38.6) * mm});
            skLineSegment(sketch, "E11.0.3.110", {"start": v(74.17, 33.53) * mm, "end": v(79.25, 38.6) * mm});
            skLineSegment(sketch, "E11.0.3.111", {"start": v(17.78, 33.53) * mm, "end": v(22.86, 38.6) * mm});
            skLineSegment(sketch, "E11.0.3.112", {"start": v(-95, 33.53) * mm, "end": v(-89.92, 38.6) * mm});
            skLineSegment(sketch, "E11.0.3.113", {"start": v(-38.6, 33.53) * mm, "end": v(-33.53, 38.6) * mm});
            skLineSegment(sketch, "E11.0.3.114", {"start": v(-22.4, 38.6) * mm, "end": v(-17.32, 33.53) * mm});
            skLineSegment(sketch, "E11.0.3.115", {"start": v(-10.41, 21.35) * mm, "end": v(-5.33, 16.27) * mm});
            skLineSegment(sketch, "E11.0.3.116", {"start": v(-66.8, 21.35) * mm, "end": v(-61.72, 16.27) * mm});
            skLineSegment(sketch, "E11.0.3.117", {"start": v(146.76, 38.6) * mm, "end": v(151.84, 33.53) * mm});
            skLineSegment(sketch, "E11.0.3.118", {"start": v(102.36, 21.35) * mm, "end": v(107.44, 16.27) * mm});
            skLineSegment(sketch, "E11.0.3.119", {"start": v(90.37, 38.6) * mm, "end": v(95.45, 33.53) * mm});
            skLineSegment(sketch, "E11.0.3.120", {"start": v(45.97, 21.35) * mm, "end": v(51.05, 16.27) * mm});
            skPoint(sketch, "E11.0.4.0", {"position": v(-73.71, 10.41) * mm});
            skLineSegment(sketch, "E11.0.4.1", {"start": v(102.36, 5.33) * mm, "end": v(102.36, -6.84) * mm});
            skLineSegment(sketch, "E11.0.4.2", {"start": v(45.97, 5.33) * mm, "end": v(45.97, -6.84) * mm});
            skPoint(sketch, "E11.0.4.3", {"position": v(39.06, 10.41) * mm});
            skLineSegment(sketch, "E11.0.4.4", {"start": v(-66.8, 5.33) * mm, "end": v(-66.8, -6.84) * mm});
            skLineSegment(sketch, "E11.0.4.5", {"start": v(-95, 5.33) * mm, "end": v(-95, -6.84) * mm});
            skLineSegment(sketch, "E11.0.4.6", {"start": v(-73.71, 5.33) * mm, "end": v(-73.71, -6.84) * mm});
            skLineSegment(sketch, "E11.0.4.7", {"start": v(-123.2, 5.33) * mm, "end": v(-123.2, -6.84) * mm});
            skLineSegment(sketch, "E11.0.4.8", {"start": v(-101.9, 5.33) * mm, "end": v(-101.9, -6.84) * mm});
            skPoint(sketch, "E11.0.4.9", {"position": v(130.56, -11.92) * mm});
            skPoint(sketch, "E11.0.4.10", {"position": v(67.26, 10.41) * mm});
            skPoint(sketch, "E11.0.4.11", {"position": v(-66.8, -11.92) * mm});
            skPoint(sketch, "E11.0.4.12", {"position": v(10.87, 10.41) * mm});
            skPoint(sketch, "E11.0.4.13", {"position": v(-101.9, -11.92) * mm});
            skPoint(sketch, "E11.0.4.14", {"position": v(45.97, -11.92) * mm});
            skLineSegment(sketch, "E11.0.4.15", {"start": v(-118.11, 10.41) * mm, "end": v(-106.99, 10.41) * mm});
            skPoint(sketch, "E11.0.4.16", {"position": v(-45.52, 10.41) * mm});
            skPoint(sketch, "E11.0.4.17", {"position": v(151.84, 10.41) * mm});
            skPoint(sketch, "E11.0.4.18", {"position": v(123.65, 10.41) * mm});
            skLineSegment(sketch, "E11.0.4.19", {"start": v(151.84, 5.33) * mm, "end": v(151.84, -6.84) * mm});
            skLineSegment(sketch, "E11.0.4.20", {"start": v(95.45, 5.33) * mm, "end": v(95.45, -6.84) * mm});
            skLineSegment(sketch, "E11.0.4.21", {"start": v(39.06, 5.33) * mm, "end": v(39.06, -6.84) * mm});
            skLineSegment(sketch, "E11.0.4.22", {"start": v(-17.32, 5.33) * mm, "end": v(-17.32, -6.84) * mm});
            skPoint(sketch, "E11.0.4.23", {"position": v(74.17, -11.92) * mm});
            skPoint(sketch, "E11.0.4.24", {"position": v(-38.6, -11.92) * mm});
            skLineSegment(sketch, "E11.0.4.25", {"start": v(-10.41, 5.33) * mm, "end": v(-10.41, -6.84) * mm});
            skLineSegment(sketch, "E11.0.4.26", {"start": v(-89.92, -11.92) * mm, "end": v(-78.8, -11.92) * mm});
            skLineSegment(sketch, "E11.0.4.27", {"start": v(-45.52, 5.33) * mm, "end": v(-45.52, -6.84) * mm});
            skLineSegment(sketch, "E11.0.4.28", {"start": v(10.87, 5.33) * mm, "end": v(10.87, -6.84) * mm});
            skPoint(sketch, "E11.0.4.29", {"position": v(-17.32, 10.41) * mm});
            skPoint(sketch, "E11.0.4.30", {"position": v(95.45, 10.41) * mm});
            skPoint(sketch, "E11.0.4.31", {"position": v(95.45, -11.92) * mm});
            skPoint(sketch, "E11.0.4.32", {"position": v(151.84, -11.92) * mm});
            skPoint(sketch, "E11.0.4.33", {"position": v(-73.71, -11.92) * mm});
            skPoint(sketch, "E11.0.4.34", {"position": v(39.06, -11.92) * mm});
            skLineSegment(sketch, "E11.0.4.35", {"start": v(67.26, 5.33) * mm, "end": v(67.26, -6.84) * mm});
            skLineSegment(sketch, "E11.0.4.36", {"start": v(123.65, 5.33) * mm, "end": v(123.65, -6.84) * mm});
            skLineSegment(sketch, "E11.0.4.37", {"start": v(-123.2, -11.92) * mm, "end": v(-95, -11.92) * mm, "construction": true});
            skPoint(sketch, "E11.0.4.38", {"position": v(130.56, 10.41) * mm});
            skPoint(sketch, "E11.0.4.39", {"position": v(45.97, 10.41) * mm});
            skLineSegment(sketch, "E11.0.4.40", {"start": v(51.05, 10.41) * mm, "end": v(62.18, 10.41) * mm});
            skPoint(sketch, "E11.0.4.41", {"position": v(-66.8, 10.41) * mm});
            skLineSegment(sketch, "E11.0.4.42", {"start": v(107.44, 10.41) * mm, "end": v(118.57, 10.41) * mm});
            skLineSegment(sketch, "E11.0.4.43", {"start": v(135.64, 10.41) * mm, "end": v(146.76, 10.41) * mm});
            skLineSegment(sketch, "E11.0.4.44", {"start": v(79.25, 10.41) * mm, "end": v(90.37, 10.41) * mm});
            skLineSegment(sketch, "E11.0.4.45", {"start": v(22.86, 10.41) * mm, "end": v(33.98, 10.41) * mm});
            skLineSegment(sketch, "E11.0.4.46", {"start": v(-33.53, 10.41) * mm, "end": v(-22.4, 10.41) * mm});
            skLineSegment(sketch, "E11.0.4.47", {"start": v(-61.72, 10.41) * mm, "end": v(-50.6, 10.41) * mm});
            skPoint(sketch, "E11.0.4.48", {"position": v(-17.32, -11.92) * mm});
            skLineSegment(sketch, "E11.0.4.49", {"start": v(-5.33, 10.41) * mm, "end": v(5.79, 10.41) * mm});
            skLineSegment(sketch, "E11.0.4.50", {"start": v(-33.53, -11.92) * mm, "end": v(-22.4, -11.92) * mm});
            skLineSegment(sketch, "E11.0.4.51", {"start": v(22.86, -11.92) * mm, "end": v(33.98, -11.92) * mm});
            skPoint(sketch, "E11.0.4.52", {"position": v(17.78, 10.41) * mm});
            skLineSegment(sketch, "E11.0.4.53", {"start": v(79.25, -11.92) * mm, "end": v(90.37, -11.92) * mm});
            skLineSegment(sketch, "E11.0.4.54", {"start": v(135.64, -11.92) * mm, "end": v(146.76, -11.92) * mm});
            skPoint(sketch, "E11.0.4.55", {"position": v(67.26, -11.92) * mm});
            skPoint(sketch, "E11.0.4.56", {"position": v(-101.9, 10.41) * mm});
            skPoint(sketch, "E11.0.4.57", {"position": v(10.87, -11.92) * mm});
            skPoint(sketch, "E11.0.4.58", {"position": v(123.65, -11.92) * mm});
            skPoint(sketch, "E11.0.4.59", {"position": v(-45.52, -11.92) * mm});
            skPoint(sketch, "E11.0.4.60", {"position": v(-95, -11.92) * mm});
            skLineSegment(sketch, "E11.0.4.61", {"start": v(51.05, -11.92) * mm, "end": v(62.18, -11.92) * mm});
            skPoint(sketch, "E11.0.4.62", {"position": v(17.78, -11.92) * mm});
            skLineSegment(sketch, "E11.0.4.63", {"start": v(107.44, -11.92) * mm, "end": v(118.57, -11.92) * mm});
            skLineSegment(sketch, "E11.0.4.64", {"start": v(-61.72, -11.92) * mm, "end": v(-50.6, -11.92) * mm});
            skLineSegment(sketch, "E11.0.4.65", {"start": v(-5.33, -11.92) * mm, "end": v(5.79, -11.92) * mm});
            skPoint(sketch, "E11.0.4.66", {"position": v(-123.2, 10.41) * mm});
            skPoint(sketch, "E11.0.4.67", {"position": v(-10.41, 10.41) * mm});
            skPoint(sketch, "E11.0.4.68", {"position": v(102.36, 10.41) * mm});
            skPoint(sketch, "E11.0.4.69", {"position": v(74.17, 10.41) * mm});
            skPoint(sketch, "E11.0.4.70", {"position": v(-10.41, -11.92) * mm});
            skPoint(sketch, "E11.0.4.71", {"position": v(102.36, -11.92) * mm});
            skPoint(sketch, "E11.0.4.72", {"position": v(-38.6, 10.41) * mm});
            skPoint(sketch, "E11.0.4.73", {"position": v(-123.2, -11.92) * mm});
            skPoint(sketch, "E11.0.4.74", {"position": v(-95, 10.41) * mm});
            skLineSegment(sketch, "E11.0.4.75", {"start": v(-38.6, 5.33) * mm, "end": v(-38.6, -6.84) * mm});
            skLineSegment(sketch, "E11.0.4.76", {"start": v(17.78, 5.33) * mm, "end": v(17.78, -6.84) * mm});
            skLineSegment(sketch, "E11.0.4.77", {"start": v(74.17, 5.33) * mm, "end": v(74.17, -6.84) * mm});
            skLineSegment(sketch, "E11.0.4.78", {"start": v(130.56, 5.33) * mm, "end": v(130.56, -6.84) * mm});
            skLineSegment(sketch, "E11.0.4.79", {"start": v(-118.11, -11.92) * mm, "end": v(-106.99, -11.92) * mm});
            skLineSegment(sketch, "E11.0.4.80", {"start": v(-89.92, 10.41) * mm, "end": v(-78.8, 10.41) * mm});
            skLineSegment(sketch, "E11.0.4.81", {"start": v(-78.8, 10.41) * mm, "end": v(-73.71, 5.33) * mm});
            skLineSegment(sketch, "E11.0.4.82", {"start": v(-95, -6.84) * mm, "end": v(-89.92, -11.92) * mm});
            skLineSegment(sketch, "E11.0.4.83", {"start": v(33.98, 10.41) * mm, "end": v(39.06, 5.33) * mm});
            skLineSegment(sketch, "E11.0.4.84", {"start": v(-73.71, -6.84) * mm, "end": v(-78.8, -11.92) * mm});
            skLineSegment(sketch, "E11.0.4.85", {"start": v(-123.2, 5.33) * mm, "end": v(-118.11, 10.41) * mm});
            skLineSegment(sketch, "E11.0.4.86", {"start": v(-106.99, 10.41) * mm, "end": v(-101.9, 5.33) * mm});
            skLineSegment(sketch, "E11.0.4.87", {"start": v(-123.2, -6.84) * mm, "end": v(-118.11, -11.92) * mm});
            skLineSegment(sketch, "E11.0.4.88", {"start": v(-101.9, -6.84) * mm, "end": v(-106.99, -11.92) * mm});
            skLineSegment(sketch, "E11.0.4.89", {"start": v(-45.52, -6.84) * mm, "end": v(-50.6, -11.92) * mm});
            skLineSegment(sketch, "E11.0.4.90", {"start": v(10.87, -6.84) * mm, "end": v(5.79, -11.92) * mm});
            skLineSegment(sketch, "E11.0.4.91", {"start": v(67.26, -6.84) * mm, "end": v(62.18, -11.92) * mm});
            skLineSegment(sketch, "E11.0.4.92", {"start": v(123.65, -6.84) * mm, "end": v(118.57, -11.92) * mm});
            skLineSegment(sketch, "E11.0.4.93", {"start": v(62.18, 10.41) * mm, "end": v(67.26, 5.33) * mm});
            skLineSegment(sketch, "E11.0.4.94", {"start": v(39.06, -6.84) * mm, "end": v(33.98, -11.92) * mm});
            skLineSegment(sketch, "E11.0.4.95", {"start": v(118.57, 10.41) * mm, "end": v(123.65, 5.33) * mm});
            skLineSegment(sketch, "E11.0.4.96", {"start": v(95.45, -6.84) * mm, "end": v(90.37, -11.92) * mm});
            skLineSegment(sketch, "E11.0.4.97", {"start": v(151.84, -6.84) * mm, "end": v(146.76, -11.92) * mm});
            skLineSegment(sketch, "E11.0.4.98", {"start": v(-50.6, 10.41) * mm, "end": v(-45.52, 5.33) * mm});
            skLineSegment(sketch, "E11.0.4.99", {"start": v(5.79, 10.41) * mm, "end": v(10.87, 5.33) * mm});
            skLineSegment(sketch, "E11.0.4.100", {"start": v(-17.32, -6.84) * mm, "end": v(-22.4, -11.92) * mm});
            skLineSegment(sketch, "E11.0.4.101", {"start": v(-38.6, -6.84) * mm, "end": v(-33.53, -11.92) * mm});
            skLineSegment(sketch, "E11.0.4.102", {"start": v(-10.41, 5.33) * mm, "end": v(-5.33, 10.41) * mm});
            skLineSegment(sketch, "E11.0.4.103", {"start": v(-66.8, 5.33) * mm, "end": v(-61.72, 10.41) * mm});
            skLineSegment(sketch, "E11.0.4.104", {"start": v(130.56, -6.84) * mm, "end": v(135.64, -11.92) * mm});
            skLineSegment(sketch, "E11.0.4.105", {"start": v(102.36, 5.33) * mm, "end": v(107.44, 10.41) * mm});
            skLineSegment(sketch, "E11.0.4.106", {"start": v(74.17, -6.84) * mm, "end": v(79.25, -11.92) * mm});
            skLineSegment(sketch, "E11.0.4.107", {"start": v(45.97, 5.33) * mm, "end": v(51.05, 10.41) * mm});
            skLineSegment(sketch, "E11.0.4.108", {"start": v(17.78, -6.84) * mm, "end": v(22.86, -11.92) * mm});
            skLineSegment(sketch, "E11.0.4.109", {"start": v(130.56, 5.33) * mm, "end": v(135.64, 10.41) * mm});
            skLineSegment(sketch, "E11.0.4.110", {"start": v(74.17, 5.33) * mm, "end": v(79.25, 10.41) * mm});
            skLineSegment(sketch, "E11.0.4.111", {"start": v(17.78, 5.33) * mm, "end": v(22.86, 10.41) * mm});
            skLineSegment(sketch, "E11.0.4.112", {"start": v(-95, 5.33) * mm, "end": v(-89.92, 10.41) * mm});
            skLineSegment(sketch, "E11.0.4.113", {"start": v(-38.6, 5.33) * mm, "end": v(-33.53, 10.41) * mm});
            skLineSegment(sketch, "E11.0.4.114", {"start": v(-22.4, 10.41) * mm, "end": v(-17.32, 5.33) * mm});
            skLineSegment(sketch, "E11.0.4.115", {"start": v(-10.41, -6.84) * mm, "end": v(-5.33, -11.92) * mm});
            skLineSegment(sketch, "E11.0.4.116", {"start": v(-66.8, -6.84) * mm, "end": v(-61.72, -11.92) * mm});
            skLineSegment(sketch, "E11.0.4.117", {"start": v(146.76, 10.41) * mm, "end": v(151.84, 5.33) * mm});
            skLineSegment(sketch, "E11.0.4.118", {"start": v(102.36, -6.84) * mm, "end": v(107.44, -11.92) * mm});
            skLineSegment(sketch, "E11.0.4.119", {"start": v(90.37, 10.41) * mm, "end": v(95.45, 5.33) * mm});
            skLineSegment(sketch, "E11.0.4.120", {"start": v(45.97, -6.84) * mm, "end": v(51.05, -11.92) * mm});
            skPoint(sketch, "E11.0.5.0", {"position": v(-73.71, -17.78) * mm});
            skLineSegment(sketch, "E11.0.5.1", {"start": v(102.36, -22.86) * mm, "end": v(102.36, -35.04) * mm});
            skLineSegment(sketch, "E11.0.5.2", {"start": v(45.97, -22.86) * mm, "end": v(45.97, -35.04) * mm});
            skPoint(sketch, "E11.0.5.3", {"position": v(39.06, -17.78) * mm});
            skLineSegment(sketch, "E11.0.5.4", {"start": v(-66.8, -22.86) * mm, "end": v(-66.8, -35.04) * mm});
            skLineSegment(sketch, "E11.0.5.5", {"start": v(-95, -22.86) * mm, "end": v(-95, -35.04) * mm});
            skLineSegment(sketch, "E11.0.5.6", {"start": v(-73.71, -22.86) * mm, "end": v(-73.71, -35.04) * mm});
            skLineSegment(sketch, "E11.0.5.7", {"start": v(-123.2, -22.86) * mm, "end": v(-123.2, -35.04) * mm});
            skLineSegment(sketch, "E11.0.5.8", {"start": v(-101.9, -22.86) * mm, "end": v(-101.9, -35.04) * mm});
            skPoint(sketch, "E11.0.5.9", {"position": v(130.56, -40.12) * mm});
            skPoint(sketch, "E11.0.5.10", {"position": v(67.26, -17.78) * mm});
            skPoint(sketch, "E11.0.5.11", {"position": v(-66.8, -40.12) * mm});
            skPoint(sketch, "E11.0.5.12", {"position": v(10.87, -17.78) * mm});
            skPoint(sketch, "E11.0.5.13", {"position": v(-101.9, -40.12) * mm});
            skPoint(sketch, "E11.0.5.14", {"position": v(45.97, -40.12) * mm});
            skLineSegment(sketch, "E11.0.5.15", {"start": v(-118.11, -17.78) * mm, "end": v(-106.99, -17.78) * mm});
            skPoint(sketch, "E11.0.5.16", {"position": v(-45.52, -17.78) * mm});
            skPoint(sketch, "E11.0.5.17", {"position": v(151.84, -17.78) * mm});
            skPoint(sketch, "E11.0.5.18", {"position": v(123.65, -17.78) * mm});
            skLineSegment(sketch, "E11.0.5.19", {"start": v(151.84, -22.86) * mm, "end": v(151.84, -35.04) * mm});
            skLineSegment(sketch, "E11.0.5.20", {"start": v(95.45, -22.86) * mm, "end": v(95.45, -35.04) * mm});
            skLineSegment(sketch, "E11.0.5.21", {"start": v(39.06, -22.86) * mm, "end": v(39.06, -35.04) * mm});
            skLineSegment(sketch, "E11.0.5.22", {"start": v(-17.32, -22.86) * mm, "end": v(-17.32, -35.04) * mm});
            skPoint(sketch, "E11.0.5.23", {"position": v(74.17, -40.12) * mm});
            skPoint(sketch, "E11.0.5.24", {"position": v(-38.6, -40.12) * mm});
            skLineSegment(sketch, "E11.0.5.25", {"start": v(-10.41, -22.86) * mm, "end": v(-10.41, -35.04) * mm});
            skLineSegment(sketch, "E11.0.5.26", {"start": v(-89.92, -40.12) * mm, "end": v(-78.8, -40.12) * mm});
            skLineSegment(sketch, "E11.0.5.27", {"start": v(-45.52, -22.86) * mm, "end": v(-45.52, -35.04) * mm});
            skLineSegment(sketch, "E11.0.5.28", {"start": v(10.87, -22.86) * mm, "end": v(10.87, -35.04) * mm});
            skPoint(sketch, "E11.0.5.29", {"position": v(-17.32, -17.78) * mm});
            skPoint(sketch, "E11.0.5.30", {"position": v(95.45, -17.78) * mm});
            skPoint(sketch, "E11.0.5.31", {"position": v(95.45, -40.12) * mm});
            skPoint(sketch, "E11.0.5.32", {"position": v(151.84, -40.12) * mm});
            skPoint(sketch, "E11.0.5.33", {"position": v(-73.71, -40.12) * mm});
            skPoint(sketch, "E11.0.5.34", {"position": v(39.06, -40.12) * mm});
            skLineSegment(sketch, "E11.0.5.35", {"start": v(67.26, -22.86) * mm, "end": v(67.26, -35.04) * mm});
            skLineSegment(sketch, "E11.0.5.36", {"start": v(123.65, -22.86) * mm, "end": v(123.65, -35.04) * mm});
            skLineSegment(sketch, "E11.0.5.37", {"start": v(-123.2, -40.12) * mm, "end": v(-95, -40.12) * mm, "construction": true});
            skPoint(sketch, "E11.0.5.38", {"position": v(130.56, -17.78) * mm});
            skPoint(sketch, "E11.0.5.39", {"position": v(45.97, -17.78) * mm});
            skLineSegment(sketch, "E11.0.5.40", {"start": v(51.05, -17.78) * mm, "end": v(62.18, -17.78) * mm});
            skPoint(sketch, "E11.0.5.41", {"position": v(-66.8, -17.78) * mm});
            skLineSegment(sketch, "E11.0.5.42", {"start": v(107.44, -17.78) * mm, "end": v(118.57, -17.78) * mm});
            skLineSegment(sketch, "E11.0.5.43", {"start": v(135.64, -17.78) * mm, "end": v(146.76, -17.78) * mm});
            skLineSegment(sketch, "E11.0.5.44", {"start": v(79.25, -17.78) * mm, "end": v(90.37, -17.78) * mm});
            skLineSegment(sketch, "E11.0.5.45", {"start": v(22.86, -17.78) * mm, "end": v(33.98, -17.78) * mm});
            skLineSegment(sketch, "E11.0.5.46", {"start": v(-33.53, -17.78) * mm, "end": v(-22.4, -17.78) * mm});
            skLineSegment(sketch, "E11.0.5.47", {"start": v(-61.72, -17.78) * mm, "end": v(-50.6, -17.78) * mm});
            skPoint(sketch, "E11.0.5.48", {"position": v(-17.32, -40.12) * mm});
            skLineSegment(sketch, "E11.0.5.49", {"start": v(-5.33, -17.78) * mm, "end": v(5.79, -17.78) * mm});
            skLineSegment(sketch, "E11.0.5.50", {"start": v(-33.53, -40.12) * mm, "end": v(-22.4, -40.12) * mm});
            skLineSegment(sketch, "E11.0.5.51", {"start": v(22.86, -40.12) * mm, "end": v(33.98, -40.12) * mm});
            skPoint(sketch, "E11.0.5.52", {"position": v(17.78, -17.78) * mm});
            skLineSegment(sketch, "E11.0.5.53", {"start": v(79.25, -40.12) * mm, "end": v(90.37, -40.12) * mm});
            skLineSegment(sketch, "E11.0.5.54", {"start": v(135.64, -40.12) * mm, "end": v(146.76, -40.12) * mm});
            skPoint(sketch, "E11.0.5.55", {"position": v(67.26, -40.12) * mm});
            skPoint(sketch, "E11.0.5.56", {"position": v(-101.9, -17.78) * mm});
            skPoint(sketch, "E11.0.5.57", {"position": v(10.87, -40.12) * mm});
            skPoint(sketch, "E11.0.5.58", {"position": v(123.65, -40.12) * mm});
            skPoint(sketch, "E11.0.5.59", {"position": v(-45.52, -40.12) * mm});
            skPoint(sketch, "E11.0.5.60", {"position": v(-95, -40.12) * mm});
            skLineSegment(sketch, "E11.0.5.61", {"start": v(51.05, -40.12) * mm, "end": v(62.18, -40.12) * mm});
            skPoint(sketch, "E11.0.5.62", {"position": v(17.78, -40.12) * mm});
            skLineSegment(sketch, "E11.0.5.63", {"start": v(107.44, -40.12) * mm, "end": v(118.57, -40.12) * mm});
            skLineSegment(sketch, "E11.0.5.64", {"start": v(-61.72, -40.12) * mm, "end": v(-50.6, -40.12) * mm});
            skLineSegment(sketch, "E11.0.5.65", {"start": v(-5.33, -40.12) * mm, "end": v(5.79, -40.12) * mm});
            skPoint(sketch, "E11.0.5.66", {"position": v(-123.2, -17.78) * mm});
            skPoint(sketch, "E11.0.5.67", {"position": v(-10.41, -17.78) * mm});
            skPoint(sketch, "E11.0.5.68", {"position": v(102.36, -17.78) * mm});
            skPoint(sketch, "E11.0.5.69", {"position": v(74.17, -17.78) * mm});
            skPoint(sketch, "E11.0.5.70", {"position": v(-10.41, -40.12) * mm});
            skPoint(sketch, "E11.0.5.71", {"position": v(102.36, -40.12) * mm});
            skPoint(sketch, "E11.0.5.72", {"position": v(-38.6, -17.78) * mm});
            skPoint(sketch, "E11.0.5.73", {"position": v(-123.2, -40.12) * mm});
            skPoint(sketch, "E11.0.5.74", {"position": v(-95, -17.78) * mm});
            skLineSegment(sketch, "E11.0.5.75", {"start": v(-38.6, -22.86) * mm, "end": v(-38.6, -35.04) * mm});
            skLineSegment(sketch, "E11.0.5.76", {"start": v(17.78, -22.86) * mm, "end": v(17.78, -35.04) * mm});
            skLineSegment(sketch, "E11.0.5.77", {"start": v(74.17, -22.86) * mm, "end": v(74.17, -35.04) * mm});
            skLineSegment(sketch, "E11.0.5.78", {"start": v(130.56, -22.86) * mm, "end": v(130.56, -35.04) * mm});
            skLineSegment(sketch, "E11.0.5.79", {"start": v(-118.11, -40.12) * mm, "end": v(-106.99, -40.12) * mm});
            skLineSegment(sketch, "E11.0.5.80", {"start": v(-89.92, -17.78) * mm, "end": v(-78.8, -17.78) * mm});
            skLineSegment(sketch, "E11.0.5.81", {"start": v(-78.8, -17.78) * mm, "end": v(-73.71, -22.86) * mm});
            skLineSegment(sketch, "E11.0.5.82", {"start": v(-95, -35.04) * mm, "end": v(-89.92, -40.12) * mm});
            skLineSegment(sketch, "E11.0.5.83", {"start": v(33.98, -17.78) * mm, "end": v(39.06, -22.86) * mm});
            skLineSegment(sketch, "E11.0.5.84", {"start": v(-73.71, -35.04) * mm, "end": v(-78.8, -40.12) * mm});
            skLineSegment(sketch, "E11.0.5.85", {"start": v(-123.2, -22.86) * mm, "end": v(-118.11, -17.78) * mm});
            skLineSegment(sketch, "E11.0.5.86", {"start": v(-106.99, -17.78) * mm, "end": v(-101.9, -22.86) * mm});
            skLineSegment(sketch, "E11.0.5.87", {"start": v(-123.2, -35.04) * mm, "end": v(-118.11, -40.12) * mm});
            skLineSegment(sketch, "E11.0.5.88", {"start": v(-101.9, -35.04) * mm, "end": v(-106.99, -40.12) * mm});
            skLineSegment(sketch, "E11.0.5.89", {"start": v(-45.52, -35.04) * mm, "end": v(-50.6, -40.12) * mm});
            skLineSegment(sketch, "E11.0.5.90", {"start": v(10.87, -35.04) * mm, "end": v(5.79, -40.12) * mm});
            skLineSegment(sketch, "E11.0.5.91", {"start": v(67.26, -35.04) * mm, "end": v(62.18, -40.12) * mm});
            skLineSegment(sketch, "E11.0.5.92", {"start": v(123.65, -35.04) * mm, "end": v(118.57, -40.12) * mm});
            skLineSegment(sketch, "E11.0.5.93", {"start": v(62.18, -17.78) * mm, "end": v(67.26, -22.86) * mm});
            skLineSegment(sketch, "E11.0.5.94", {"start": v(39.06, -35.04) * mm, "end": v(33.98, -40.12) * mm});
            skLineSegment(sketch, "E11.0.5.95", {"start": v(118.57, -17.78) * mm, "end": v(123.65, -22.86) * mm});
            skLineSegment(sketch, "E11.0.5.96", {"start": v(95.45, -35.04) * mm, "end": v(90.37, -40.12) * mm});
            skLineSegment(sketch, "E11.0.5.97", {"start": v(151.84, -35.04) * mm, "end": v(146.76, -40.12) * mm});
            skLineSegment(sketch, "E11.0.5.98", {"start": v(-50.6, -17.78) * mm, "end": v(-45.52, -22.86) * mm});
            skLineSegment(sketch, "E11.0.5.99", {"start": v(5.79, -17.78) * mm, "end": v(10.87, -22.86) * mm});
            skLineSegment(sketch, "E11.0.5.100", {"start": v(-17.32, -35.04) * mm, "end": v(-22.4, -40.12) * mm});
            skLineSegment(sketch, "E11.0.5.101", {"start": v(-38.6, -35.04) * mm, "end": v(-33.53, -40.12) * mm});
            skLineSegment(sketch, "E11.0.5.102", {"start": v(-10.41, -22.86) * mm, "end": v(-5.33, -17.78) * mm});
            skLineSegment(sketch, "E11.0.5.103", {"start": v(-66.8, -22.86) * mm, "end": v(-61.72, -17.78) * mm});
            skLineSegment(sketch, "E11.0.5.104", {"start": v(130.56, -35.04) * mm, "end": v(135.64, -40.12) * mm});
            skLineSegment(sketch, "E11.0.5.105", {"start": v(102.36, -22.86) * mm, "end": v(107.44, -17.78) * mm});
            skLineSegment(sketch, "E11.0.5.106", {"start": v(74.17, -35.04) * mm, "end": v(79.25, -40.12) * mm});
            skLineSegment(sketch, "E11.0.5.107", {"start": v(45.97, -22.86) * mm, "end": v(51.05, -17.78) * mm});
            skLineSegment(sketch, "E11.0.5.108", {"start": v(17.78, -35.04) * mm, "end": v(22.86, -40.12) * mm});
            skLineSegment(sketch, "E11.0.5.109", {"start": v(130.56, -22.86) * mm, "end": v(135.64, -17.78) * mm});
            skLineSegment(sketch, "E11.0.5.110", {"start": v(74.17, -22.86) * mm, "end": v(79.25, -17.78) * mm});
            skLineSegment(sketch, "E11.0.5.111", {"start": v(17.78, -22.86) * mm, "end": v(22.86, -17.78) * mm});
            skLineSegment(sketch, "E11.0.5.112", {"start": v(-95, -22.86) * mm, "end": v(-89.92, -17.78) * mm});
            skLineSegment(sketch, "E11.0.5.113", {"start": v(-38.6, -22.86) * mm, "end": v(-33.53, -17.78) * mm});
            skLineSegment(sketch, "E11.0.5.114", {"start": v(-22.4, -17.78) * mm, "end": v(-17.32, -22.86) * mm});
            skLineSegment(sketch, "E11.0.5.115", {"start": v(-10.41, -35.04) * mm, "end": v(-5.33, -40.12) * mm});
            skLineSegment(sketch, "E11.0.5.116", {"start": v(-66.8, -35.04) * mm, "end": v(-61.72, -40.12) * mm});
            skLineSegment(sketch, "E11.0.5.117", {"start": v(146.76, -17.78) * mm, "end": v(151.84, -22.86) * mm});
            skLineSegment(sketch, "E11.0.5.118", {"start": v(102.36, -35.04) * mm, "end": v(107.44, -40.12) * mm});
            skLineSegment(sketch, "E11.0.5.119", {"start": v(90.37, -17.78) * mm, "end": v(95.45, -22.86) * mm});
            skLineSegment(sketch, "E11.0.5.120", {"start": v(45.97, -35.04) * mm, "end": v(51.05, -40.12) * mm});
            skPoint(sketch, "E11.0.6.0", {"position": v(-73.71, -45.97) * mm});
            skLineSegment(sketch, "E11.0.6.1", {"start": v(102.36, -51.05) * mm, "end": v(102.36, -63.23) * mm});
            skLineSegment(sketch, "E11.0.6.2", {"start": v(45.97, -51.05) * mm, "end": v(45.97, -63.23) * mm});
            skPoint(sketch, "E11.0.6.3", {"position": v(39.06, -45.97) * mm});
            skLineSegment(sketch, "E11.0.6.4", {"start": v(-66.8, -51.05) * mm, "end": v(-66.8, -63.23) * mm});
            skLineSegment(sketch, "E11.0.6.5", {"start": v(-95, -51.05) * mm, "end": v(-95, -63.23) * mm});
            skLineSegment(sketch, "E11.0.6.6", {"start": v(-73.71, -51.05) * mm, "end": v(-73.71, -63.23) * mm});
            skLineSegment(sketch, "E11.0.6.7", {"start": v(-123.2, -51.05) * mm, "end": v(-123.2, -63.23) * mm});
            skLineSegment(sketch, "E11.0.6.8", {"start": v(-101.9, -51.05) * mm, "end": v(-101.9, -63.23) * mm});
            skPoint(sketch, "E11.0.6.9", {"position": v(130.56, -68.3) * mm});
            skPoint(sketch, "E11.0.6.10", {"position": v(67.26, -45.97) * mm});
            skPoint(sketch, "E11.0.6.11", {"position": v(-66.8, -68.3) * mm});
            skPoint(sketch, "E11.0.6.12", {"position": v(10.87, -45.97) * mm});
            skPoint(sketch, "E11.0.6.13", {"position": v(-101.9, -68.3) * mm});
            skPoint(sketch, "E11.0.6.14", {"position": v(45.97, -68.3) * mm});
            skLineSegment(sketch, "E11.0.6.15", {"start": v(-118.11, -45.97) * mm, "end": v(-106.99, -45.97) * mm});
            skPoint(sketch, "E11.0.6.16", {"position": v(-45.52, -45.97) * mm});
            skPoint(sketch, "E11.0.6.17", {"position": v(151.84, -45.97) * mm});
            skPoint(sketch, "E11.0.6.18", {"position": v(123.65, -45.97) * mm});
            skLineSegment(sketch, "E11.0.6.19", {"start": v(151.84, -51.05) * mm, "end": v(151.84, -63.23) * mm});
            skLineSegment(sketch, "E11.0.6.20", {"start": v(95.45, -51.05) * mm, "end": v(95.45, -63.23) * mm});
            skLineSegment(sketch, "E11.0.6.21", {"start": v(39.06, -51.05) * mm, "end": v(39.06, -63.23) * mm});
            skLineSegment(sketch, "E11.0.6.22", {"start": v(-17.32, -51.05) * mm, "end": v(-17.32, -63.23) * mm});
            skPoint(sketch, "E11.0.6.23", {"position": v(74.17, -68.3) * mm});
            skPoint(sketch, "E11.0.6.24", {"position": v(-38.6, -68.3) * mm});
            skLineSegment(sketch, "E11.0.6.25", {"start": v(-10.41, -51.05) * mm, "end": v(-10.41, -63.23) * mm});
            skLineSegment(sketch, "E11.0.6.26", {"start": v(-89.92, -68.3) * mm, "end": v(-78.8, -68.3) * mm});
            skLineSegment(sketch, "E11.0.6.27", {"start": v(-45.52, -51.05) * mm, "end": v(-45.52, -63.23) * mm});
            skLineSegment(sketch, "E11.0.6.28", {"start": v(10.87, -51.05) * mm, "end": v(10.87, -63.23) * mm});
            skPoint(sketch, "E11.0.6.29", {"position": v(-17.32, -45.97) * mm});
            skPoint(sketch, "E11.0.6.30", {"position": v(95.45, -45.97) * mm});
            skPoint(sketch, "E11.0.6.31", {"position": v(95.45, -68.3) * mm});
            skPoint(sketch, "E11.0.6.32", {"position": v(151.84, -68.3) * mm});
            skPoint(sketch, "E11.0.6.33", {"position": v(-73.71, -68.3) * mm});
            skPoint(sketch, "E11.0.6.34", {"position": v(39.06, -68.3) * mm});
            skLineSegment(sketch, "E11.0.6.35", {"start": v(67.26, -51.05) * mm, "end": v(67.26, -63.23) * mm});
            skLineSegment(sketch, "E11.0.6.36", {"start": v(123.65, -51.05) * mm, "end": v(123.65, -63.23) * mm});
            skLineSegment(sketch, "E11.0.6.37", {"start": v(-123.2, -68.3) * mm, "end": v(-95, -68.3) * mm, "construction": true});
            skPoint(sketch, "E11.0.6.38", {"position": v(130.56, -45.97) * mm});
            skPoint(sketch, "E11.0.6.39", {"position": v(45.97, -45.97) * mm});
            skLineSegment(sketch, "E11.0.6.40", {"start": v(51.05, -45.97) * mm, "end": v(62.18, -45.97) * mm});
            skPoint(sketch, "E11.0.6.41", {"position": v(-66.8, -45.97) * mm});
            skLineSegment(sketch, "E11.0.6.42", {"start": v(107.44, -45.97) * mm, "end": v(118.57, -45.97) * mm});
            skLineSegment(sketch, "E11.0.6.43", {"start": v(135.64, -45.97) * mm, "end": v(146.76, -45.97) * mm});
            skLineSegment(sketch, "E11.0.6.44", {"start": v(79.25, -45.97) * mm, "end": v(90.37, -45.97) * mm});
            skLineSegment(sketch, "E11.0.6.45", {"start": v(22.86, -45.97) * mm, "end": v(33.98, -45.97) * mm});
            skLineSegment(sketch, "E11.0.6.46", {"start": v(-33.53, -45.97) * mm, "end": v(-22.4, -45.97) * mm});
            skLineSegment(sketch, "E11.0.6.47", {"start": v(-61.72, -45.97) * mm, "end": v(-50.6, -45.97) * mm});
            skPoint(sketch, "E11.0.6.48", {"position": v(-17.32, -68.3) * mm});
            skLineSegment(sketch, "E11.0.6.49", {"start": v(-5.33, -45.97) * mm, "end": v(5.79, -45.97) * mm});
            skLineSegment(sketch, "E11.0.6.50", {"start": v(-33.53, -68.3) * mm, "end": v(-22.4, -68.3) * mm});
            skLineSegment(sketch, "E11.0.6.51", {"start": v(22.86, -68.3) * mm, "end": v(33.98, -68.3) * mm});
            skPoint(sketch, "E11.0.6.52", {"position": v(17.78, -45.97) * mm});
            skLineSegment(sketch, "E11.0.6.53", {"start": v(79.25, -68.3) * mm, "end": v(90.37, -68.3) * mm});
            skLineSegment(sketch, "E11.0.6.54", {"start": v(135.64, -68.3) * mm, "end": v(146.76, -68.3) * mm});
            skPoint(sketch, "E11.0.6.55", {"position": v(67.26, -68.3) * mm});
            skPoint(sketch, "E11.0.6.56", {"position": v(-101.9, -45.97) * mm});
            skPoint(sketch, "E11.0.6.57", {"position": v(10.87, -68.3) * mm});
            skPoint(sketch, "E11.0.6.58", {"position": v(123.65, -68.3) * mm});
            skPoint(sketch, "E11.0.6.59", {"position": v(-45.52, -68.3) * mm});
            skPoint(sketch, "E11.0.6.60", {"position": v(-95, -68.3) * mm});
            skLineSegment(sketch, "E11.0.6.61", {"start": v(51.05, -68.3) * mm, "end": v(62.18, -68.3) * mm});
            skPoint(sketch, "E11.0.6.62", {"position": v(17.78, -68.3) * mm});
            skLineSegment(sketch, "E11.0.6.63", {"start": v(107.44, -68.3) * mm, "end": v(118.57, -68.3) * mm});
            skLineSegment(sketch, "E11.0.6.64", {"start": v(-61.72, -68.3) * mm, "end": v(-50.6, -68.3) * mm});
            skLineSegment(sketch, "E11.0.6.65", {"start": v(-5.33, -68.3) * mm, "end": v(5.79, -68.3) * mm});
            skPoint(sketch, "E11.0.6.66", {"position": v(-123.2, -45.97) * mm});
            skPoint(sketch, "E11.0.6.67", {"position": v(-10.41, -45.97) * mm});
            skPoint(sketch, "E11.0.6.68", {"position": v(102.36, -45.97) * mm});
            skPoint(sketch, "E11.0.6.69", {"position": v(74.17, -45.97) * mm});
            skPoint(sketch, "E11.0.6.70", {"position": v(-10.41, -68.3) * mm});
            skPoint(sketch, "E11.0.6.71", {"position": v(102.36, -68.3) * mm});
            skPoint(sketch, "E11.0.6.72", {"position": v(-38.6, -45.97) * mm});
            skPoint(sketch, "E11.0.6.73", {"position": v(-123.2, -68.3) * mm});
            skPoint(sketch, "E11.0.6.74", {"position": v(-95, -45.97) * mm});
            skLineSegment(sketch, "E11.0.6.75", {"start": v(-38.6, -51.05) * mm, "end": v(-38.6, -63.23) * mm});
            skLineSegment(sketch, "E11.0.6.76", {"start": v(17.78, -51.05) * mm, "end": v(17.78, -63.23) * mm});
            skLineSegment(sketch, "E11.0.6.77", {"start": v(74.17, -51.05) * mm, "end": v(74.17, -63.23) * mm});
            skLineSegment(sketch, "E11.0.6.78", {"start": v(130.56, -51.05) * mm, "end": v(130.56, -63.23) * mm});
            skLineSegment(sketch, "E11.0.6.79", {"start": v(-118.11, -68.3) * mm, "end": v(-106.99, -68.3) * mm});
            skLineSegment(sketch, "E11.0.6.80", {"start": v(-89.92, -45.97) * mm, "end": v(-78.8, -45.97) * mm});
            skLineSegment(sketch, "E11.0.6.81", {"start": v(-78.8, -45.97) * mm, "end": v(-73.71, -51.05) * mm});
            skLineSegment(sketch, "E11.0.6.82", {"start": v(-95, -63.23) * mm, "end": v(-89.92, -68.3) * mm});
            skLineSegment(sketch, "E11.0.6.83", {"start": v(33.98, -45.97) * mm, "end": v(39.06, -51.05) * mm});
            skLineSegment(sketch, "E11.0.6.84", {"start": v(-73.71, -63.23) * mm, "end": v(-78.8, -68.3) * mm});
            skLineSegment(sketch, "E11.0.6.85", {"start": v(-123.2, -51.05) * mm, "end": v(-118.11, -45.97) * mm});
            skLineSegment(sketch, "E11.0.6.86", {"start": v(-106.99, -45.97) * mm, "end": v(-101.9, -51.05) * mm});
            skLineSegment(sketch, "E11.0.6.87", {"start": v(-123.2, -63.23) * mm, "end": v(-118.11, -68.3) * mm});
            skLineSegment(sketch, "E11.0.6.88", {"start": v(-101.9, -63.23) * mm, "end": v(-106.99, -68.3) * mm});
            skLineSegment(sketch, "E11.0.6.89", {"start": v(-45.52, -63.23) * mm, "end": v(-50.6, -68.3) * mm});
            skLineSegment(sketch, "E11.0.6.90", {"start": v(10.87, -63.23) * mm, "end": v(5.79, -68.3) * mm});
            skLineSegment(sketch, "E11.0.6.91", {"start": v(67.26, -63.23) * mm, "end": v(62.18, -68.3) * mm});
            skLineSegment(sketch, "E11.0.6.92", {"start": v(123.65, -63.23) * mm, "end": v(118.57, -68.3) * mm});
            skLineSegment(sketch, "E11.0.6.93", {"start": v(62.18, -45.97) * mm, "end": v(67.26, -51.05) * mm});
            skLineSegment(sketch, "E11.0.6.94", {"start": v(39.06, -63.23) * mm, "end": v(33.98, -68.3) * mm});
            skLineSegment(sketch, "E11.0.6.95", {"start": v(118.57, -45.97) * mm, "end": v(123.65, -51.05) * mm});
            skLineSegment(sketch, "E11.0.6.96", {"start": v(95.45, -63.23) * mm, "end": v(90.37, -68.3) * mm});
            skLineSegment(sketch, "E11.0.6.97", {"start": v(151.84, -63.23) * mm, "end": v(146.76, -68.3) * mm});
            skLineSegment(sketch, "E11.0.6.98", {"start": v(-50.6, -45.97) * mm, "end": v(-45.52, -51.05) * mm});
            skLineSegment(sketch, "E11.0.6.99", {"start": v(5.79, -45.97) * mm, "end": v(10.87, -51.05) * mm});
            skLineSegment(sketch, "E11.0.6.100", {"start": v(-17.32, -63.23) * mm, "end": v(-22.4, -68.3) * mm});
            skLineSegment(sketch, "E11.0.6.101", {"start": v(-38.6, -63.23) * mm, "end": v(-33.53, -68.3) * mm});
            skLineSegment(sketch, "E11.0.6.102", {"start": v(-10.41, -51.05) * mm, "end": v(-5.33, -45.97) * mm});
            skLineSegment(sketch, "E11.0.6.103", {"start": v(-66.8, -51.05) * mm, "end": v(-61.72, -45.97) * mm});
            skLineSegment(sketch, "E11.0.6.104", {"start": v(130.56, -63.23) * mm, "end": v(135.64, -68.3) * mm});
            skLineSegment(sketch, "E11.0.6.105", {"start": v(102.36, -51.05) * mm, "end": v(107.44, -45.97) * mm});
            skLineSegment(sketch, "E11.0.6.106", {"start": v(74.17, -63.23) * mm, "end": v(79.25, -68.3) * mm});
            skLineSegment(sketch, "E11.0.6.107", {"start": v(45.97, -51.05) * mm, "end": v(51.05, -45.97) * mm});
            skLineSegment(sketch, "E11.0.6.108", {"start": v(17.78, -63.23) * mm, "end": v(22.86, -68.3) * mm});
            skLineSegment(sketch, "E11.0.6.109", {"start": v(130.56, -51.05) * mm, "end": v(135.64, -45.97) * mm});
            skLineSegment(sketch, "E11.0.6.110", {"start": v(74.17, -51.05) * mm, "end": v(79.25, -45.97) * mm});
            skLineSegment(sketch, "E11.0.6.111", {"start": v(17.78, -51.05) * mm, "end": v(22.86, -45.97) * mm});
            skLineSegment(sketch, "E11.0.6.112", {"start": v(-95, -51.05) * mm, "end": v(-89.92, -45.97) * mm});
            skLineSegment(sketch, "E11.0.6.113", {"start": v(-38.6, -51.05) * mm, "end": v(-33.53, -45.97) * mm});
            skLineSegment(sketch, "E11.0.6.114", {"start": v(-22.4, -45.97) * mm, "end": v(-17.32, -51.05) * mm});
            skLineSegment(sketch, "E11.0.6.115", {"start": v(-10.41, -63.23) * mm, "end": v(-5.33, -68.3) * mm});
            skLineSegment(sketch, "E11.0.6.116", {"start": v(-66.8, -63.23) * mm, "end": v(-61.72, -68.3) * mm});
            skLineSegment(sketch, "E11.0.6.117", {"start": v(146.76, -45.97) * mm, "end": v(151.84, -51.05) * mm});
            skLineSegment(sketch, "E11.0.6.118", {"start": v(102.36, -63.23) * mm, "end": v(107.44, -68.3) * mm});
            skLineSegment(sketch, "E11.0.6.119", {"start": v(90.37, -45.97) * mm, "end": v(95.45, -51.05) * mm});
            skLineSegment(sketch, "E11.0.6.120", {"start": v(45.97, -63.23) * mm, "end": v(51.05, -68.3) * mm});
            skPoint(sketch, "E11.0.7.0", {"position": v(-73.71, -74.17) * mm});
            skLineSegment(sketch, "E11.0.7.1", {"start": v(102.36, -79.25) * mm, "end": v(102.36, -91.42) * mm});
            skLineSegment(sketch, "E11.0.7.2", {"start": v(45.97, -79.25) * mm, "end": v(45.97, -91.42) * mm});
            skPoint(sketch, "E11.0.7.3", {"position": v(39.06, -74.17) * mm});
            skLineSegment(sketch, "E11.0.7.4", {"start": v(-66.8, -79.25) * mm, "end": v(-66.8, -91.42) * mm});
            skLineSegment(sketch, "E11.0.7.5", {"start": v(-95, -79.25) * mm, "end": v(-95, -91.42) * mm});
            skLineSegment(sketch, "E11.0.7.6", {"start": v(-73.71, -79.25) * mm, "end": v(-73.71, -91.42) * mm});
            skLineSegment(sketch, "E11.0.7.7", {"start": v(-123.2, -79.25) * mm, "end": v(-123.2, -91.42) * mm});
            skLineSegment(sketch, "E11.0.7.8", {"start": v(-101.9, -79.25) * mm, "end": v(-101.9, -91.42) * mm});
            skPoint(sketch, "E11.0.7.9", {"position": v(130.56, -96.5) * mm});
            skPoint(sketch, "E11.0.7.10", {"position": v(67.26, -74.17) * mm});
            skPoint(sketch, "E11.0.7.11", {"position": v(-66.8, -96.5) * mm});
            skPoint(sketch, "E11.0.7.12", {"position": v(10.87, -74.17) * mm});
            skPoint(sketch, "E11.0.7.13", {"position": v(-101.9, -96.5) * mm});
            skPoint(sketch, "E11.0.7.14", {"position": v(45.97, -96.5) * mm});
            skLineSegment(sketch, "E11.0.7.15", {"start": v(-118.11, -74.17) * mm, "end": v(-106.99, -74.17) * mm});
            skPoint(sketch, "E11.0.7.16", {"position": v(-45.52, -74.17) * mm});
            skPoint(sketch, "E11.0.7.17", {"position": v(151.84, -74.17) * mm});
            skPoint(sketch, "E11.0.7.18", {"position": v(123.65, -74.17) * mm});
            skLineSegment(sketch, "E11.0.7.19", {"start": v(151.84, -79.25) * mm, "end": v(151.84, -91.42) * mm});
            skLineSegment(sketch, "E11.0.7.20", {"start": v(95.45, -79.25) * mm, "end": v(95.45, -91.42) * mm});
            skLineSegment(sketch, "E11.0.7.21", {"start": v(39.06, -79.25) * mm, "end": v(39.06, -91.42) * mm});
            skLineSegment(sketch, "E11.0.7.22", {"start": v(-17.32, -79.25) * mm, "end": v(-17.32, -91.42) * mm});
            skPoint(sketch, "E11.0.7.23", {"position": v(74.17, -96.5) * mm});
            skPoint(sketch, "E11.0.7.24", {"position": v(-38.6, -96.5) * mm});
            skLineSegment(sketch, "E11.0.7.25", {"start": v(-10.41, -79.25) * mm, "end": v(-10.41, -91.42) * mm});
            skLineSegment(sketch, "E11.0.7.26", {"start": v(-89.92, -96.5) * mm, "end": v(-78.8, -96.5) * mm});
            skLineSegment(sketch, "E11.0.7.27", {"start": v(-45.52, -79.25) * mm, "end": v(-45.52, -91.42) * mm});
            skLineSegment(sketch, "E11.0.7.28", {"start": v(10.87, -79.25) * mm, "end": v(10.87, -91.42) * mm});
            skPoint(sketch, "E11.0.7.29", {"position": v(-17.32, -74.17) * mm});
            skPoint(sketch, "E11.0.7.30", {"position": v(95.45, -74.17) * mm});
            skPoint(sketch, "E11.0.7.31", {"position": v(95.45, -96.5) * mm});
            skPoint(sketch, "E11.0.7.32", {"position": v(151.84, -96.5) * mm});
            skPoint(sketch, "E11.0.7.33", {"position": v(-73.71, -96.5) * mm});
            skPoint(sketch, "E11.0.7.34", {"position": v(39.06, -96.5) * mm});
            skLineSegment(sketch, "E11.0.7.35", {"start": v(67.26, -79.25) * mm, "end": v(67.26, -91.42) * mm});
            skLineSegment(sketch, "E11.0.7.36", {"start": v(123.65, -79.25) * mm, "end": v(123.65, -91.42) * mm});
            skLineSegment(sketch, "E11.0.7.37", {"start": v(-123.2, -96.5) * mm, "end": v(-95, -96.5) * mm, "construction": true});
            skPoint(sketch, "E11.0.7.38", {"position": v(130.56, -74.17) * mm});
            skPoint(sketch, "E11.0.7.39", {"position": v(45.97, -74.17) * mm});
            skLineSegment(sketch, "E11.0.7.40", {"start": v(51.05, -74.17) * mm, "end": v(62.18, -74.17) * mm});
            skPoint(sketch, "E11.0.7.41", {"position": v(-66.8, -74.17) * mm});
            skLineSegment(sketch, "E11.0.7.42", {"start": v(107.44, -74.17) * mm, "end": v(118.57, -74.17) * mm});
            skLineSegment(sketch, "E11.0.7.43", {"start": v(135.64, -74.17) * mm, "end": v(146.76, -74.17) * mm});
            skLineSegment(sketch, "E11.0.7.44", {"start": v(79.25, -74.17) * mm, "end": v(90.37, -74.17) * mm});
            skLineSegment(sketch, "E11.0.7.45", {"start": v(22.86, -74.17) * mm, "end": v(33.98, -74.17) * mm});
            skLineSegment(sketch, "E11.0.7.46", {"start": v(-33.53, -74.17) * mm, "end": v(-22.4, -74.17) * mm});
            skLineSegment(sketch, "E11.0.7.47", {"start": v(-61.72, -74.17) * mm, "end": v(-50.6, -74.17) * mm});
            skPoint(sketch, "E11.0.7.48", {"position": v(-17.32, -96.5) * mm});
            skLineSegment(sketch, "E11.0.7.49", {"start": v(-5.33, -74.17) * mm, "end": v(5.79, -74.17) * mm});
            skLineSegment(sketch, "E11.0.7.50", {"start": v(-33.53, -96.5) * mm, "end": v(-22.4, -96.5) * mm});
            skLineSegment(sketch, "E11.0.7.51", {"start": v(22.86, -96.5) * mm, "end": v(33.98, -96.5) * mm});
            skPoint(sketch, "E11.0.7.52", {"position": v(17.78, -74.17) * mm});
            skLineSegment(sketch, "E11.0.7.53", {"start": v(79.25, -96.5) * mm, "end": v(90.37, -96.5) * mm});
            skLineSegment(sketch, "E11.0.7.54", {"start": v(135.64, -96.5) * mm, "end": v(146.76, -96.5) * mm});
            skPoint(sketch, "E11.0.7.55", {"position": v(67.26, -96.5) * mm});
            skPoint(sketch, "E11.0.7.56", {"position": v(-101.9, -74.17) * mm});
            skPoint(sketch, "E11.0.7.57", {"position": v(10.87, -96.5) * mm});
            skPoint(sketch, "E11.0.7.58", {"position": v(123.65, -96.5) * mm});
            skPoint(sketch, "E11.0.7.59", {"position": v(-45.52, -96.5) * mm});
            skPoint(sketch, "E11.0.7.60", {"position": v(-95, -96.5) * mm});
            skLineSegment(sketch, "E11.0.7.61", {"start": v(51.05, -96.5) * mm, "end": v(62.18, -96.5) * mm});
            skPoint(sketch, "E11.0.7.62", {"position": v(17.78, -96.5) * mm});
            skLineSegment(sketch, "E11.0.7.63", {"start": v(107.44, -96.5) * mm, "end": v(118.57, -96.5) * mm});
            skLineSegment(sketch, "E11.0.7.64", {"start": v(-61.72, -96.5) * mm, "end": v(-50.6, -96.5) * mm});
            skLineSegment(sketch, "E11.0.7.65", {"start": v(-5.33, -96.5) * mm, "end": v(5.79, -96.5) * mm});
            skPoint(sketch, "E11.0.7.66", {"position": v(-123.2, -74.17) * mm});
            skPoint(sketch, "E11.0.7.67", {"position": v(-10.41, -74.17) * mm});
            skPoint(sketch, "E11.0.7.68", {"position": v(102.36, -74.17) * mm});
            skPoint(sketch, "E11.0.7.69", {"position": v(74.17, -74.17) * mm});
            skPoint(sketch, "E11.0.7.70", {"position": v(-10.41, -96.5) * mm});
            skPoint(sketch, "E11.0.7.71", {"position": v(102.36, -96.5) * mm});
            skPoint(sketch, "E11.0.7.72", {"position": v(-38.6, -74.17) * mm});
            skPoint(sketch, "E11.0.7.73", {"position": v(-123.2, -96.5) * mm});
            skPoint(sketch, "E11.0.7.74", {"position": v(-95, -74.17) * mm});
            skLineSegment(sketch, "E11.0.7.75", {"start": v(-38.6, -79.25) * mm, "end": v(-38.6, -91.42) * mm});
            skLineSegment(sketch, "E11.0.7.76", {"start": v(17.78, -79.25) * mm, "end": v(17.78, -91.42) * mm});
            skLineSegment(sketch, "E11.0.7.77", {"start": v(74.17, -79.25) * mm, "end": v(74.17, -91.42) * mm});
            skLineSegment(sketch, "E11.0.7.78", {"start": v(130.56, -79.25) * mm, "end": v(130.56, -91.42) * mm});
            skLineSegment(sketch, "E11.0.7.79", {"start": v(-118.11, -96.5) * mm, "end": v(-106.99, -96.5) * mm});
            skLineSegment(sketch, "E11.0.7.80", {"start": v(-89.92, -74.17) * mm, "end": v(-78.8, -74.17) * mm});
            skLineSegment(sketch, "E11.0.7.81", {"start": v(-78.8, -74.17) * mm, "end": v(-73.71, -79.25) * mm});
            skLineSegment(sketch, "E11.0.7.82", {"start": v(-95, -91.42) * mm, "end": v(-89.92, -96.5) * mm});
            skLineSegment(sketch, "E11.0.7.83", {"start": v(33.98, -74.17) * mm, "end": v(39.06, -79.25) * mm});
            skLineSegment(sketch, "E11.0.7.84", {"start": v(-73.71, -91.42) * mm, "end": v(-78.8, -96.5) * mm});
            skLineSegment(sketch, "E11.0.7.85", {"start": v(-123.2, -79.25) * mm, "end": v(-118.11, -74.17) * mm});
            skLineSegment(sketch, "E11.0.7.86", {"start": v(-106.99, -74.17) * mm, "end": v(-101.9, -79.25) * mm});
            skLineSegment(sketch, "E11.0.7.87", {"start": v(-123.2, -91.42) * mm, "end": v(-118.11, -96.5) * mm});
            skLineSegment(sketch, "E11.0.7.88", {"start": v(-101.9, -91.42) * mm, "end": v(-106.99, -96.5) * mm});
            skLineSegment(sketch, "E11.0.7.89", {"start": v(-45.52, -91.42) * mm, "end": v(-50.6, -96.5) * mm});
            skLineSegment(sketch, "E11.0.7.90", {"start": v(10.87, -91.42) * mm, "end": v(5.79, -96.5) * mm});
            skLineSegment(sketch, "E11.0.7.91", {"start": v(67.26, -91.42) * mm, "end": v(62.18, -96.5) * mm});
            skLineSegment(sketch, "E11.0.7.92", {"start": v(123.65, -91.42) * mm, "end": v(118.57, -96.5) * mm});
            skLineSegment(sketch, "E11.0.7.93", {"start": v(62.18, -74.17) * mm, "end": v(67.26, -79.25) * mm});
            skLineSegment(sketch, "E11.0.7.94", {"start": v(39.06, -91.42) * mm, "end": v(33.98, -96.5) * mm});
            skLineSegment(sketch, "E11.0.7.95", {"start": v(118.57, -74.17) * mm, "end": v(123.65, -79.25) * mm});
            skLineSegment(sketch, "E11.0.7.96", {"start": v(95.45, -91.42) * mm, "end": v(90.37, -96.5) * mm});
            skLineSegment(sketch, "E11.0.7.97", {"start": v(151.84, -91.42) * mm, "end": v(146.76, -96.5) * mm});
            skLineSegment(sketch, "E11.0.7.98", {"start": v(-50.6, -74.17) * mm, "end": v(-45.52, -79.25) * mm});
            skLineSegment(sketch, "E11.0.7.99", {"start": v(5.79, -74.17) * mm, "end": v(10.87, -79.25) * mm});
            skLineSegment(sketch, "E11.0.7.100", {"start": v(-17.32, -91.42) * mm, "end": v(-22.4, -96.5) * mm});
            skLineSegment(sketch, "E11.0.7.101", {"start": v(-38.6, -91.42) * mm, "end": v(-33.53, -96.5) * mm});
            skLineSegment(sketch, "E11.0.7.102", {"start": v(-10.41, -79.25) * mm, "end": v(-5.33, -74.17) * mm});
            skLineSegment(sketch, "E11.0.7.103", {"start": v(-66.8, -79.25) * mm, "end": v(-61.72, -74.17) * mm});
            skLineSegment(sketch, "E11.0.7.104", {"start": v(130.56, -91.42) * mm, "end": v(135.64, -96.5) * mm});
            skLineSegment(sketch, "E11.0.7.105", {"start": v(102.36, -79.25) * mm, "end": v(107.44, -74.17) * mm});
            skLineSegment(sketch, "E11.0.7.106", {"start": v(74.17, -91.42) * mm, "end": v(79.25, -96.5) * mm});
            skLineSegment(sketch, "E11.0.7.107", {"start": v(45.97, -79.25) * mm, "end": v(51.05, -74.17) * mm});
            skLineSegment(sketch, "E11.0.7.108", {"start": v(17.78, -91.42) * mm, "end": v(22.86, -96.5) * mm});
            skLineSegment(sketch, "E11.0.7.109", {"start": v(130.56, -79.25) * mm, "end": v(135.64, -74.17) * mm});
            skLineSegment(sketch, "E11.0.7.110", {"start": v(74.17, -79.25) * mm, "end": v(79.25, -74.17) * mm});
            skLineSegment(sketch, "E11.0.7.111", {"start": v(17.78, -79.25) * mm, "end": v(22.86, -74.17) * mm});
            skLineSegment(sketch, "E11.0.7.112", {"start": v(-95, -79.25) * mm, "end": v(-89.92, -74.17) * mm});
            skLineSegment(sketch, "E11.0.7.113", {"start": v(-38.6, -79.25) * mm, "end": v(-33.53, -74.17) * mm});
            skLineSegment(sketch, "E11.0.7.114", {"start": v(-22.4, -74.17) * mm, "end": v(-17.32, -79.25) * mm});
            skLineSegment(sketch, "E11.0.7.115", {"start": v(-10.41, -91.42) * mm, "end": v(-5.33, -96.5) * mm});
            skLineSegment(sketch, "E11.0.7.116", {"start": v(-66.8, -91.42) * mm, "end": v(-61.72, -96.5) * mm});
            skLineSegment(sketch, "E11.0.7.117", {"start": v(146.76, -74.17) * mm, "end": v(151.84, -79.25) * mm});
            skLineSegment(sketch, "E11.0.7.118", {"start": v(102.36, -91.42) * mm, "end": v(107.44, -96.5) * mm});
            skLineSegment(sketch, "E11.0.7.119", {"start": v(90.37, -74.17) * mm, "end": v(95.45, -79.25) * mm});
            skLineSegment(sketch, "E11.0.7.120", {"start": v(45.97, -91.42) * mm, "end": v(51.05, -96.5) * mm});
            skPoint(sketch, "E11.0.8.0", {"position": v(-73.71, -102.36) * mm});
            skLineSegment(sketch, "E11.0.8.1", {"start": v(102.36, -107.44) * mm, "end": v(102.36, -119.62) * mm});
            skLineSegment(sketch, "E11.0.8.2", {"start": v(45.97, -107.44) * mm, "end": v(45.97, -119.62) * mm});
            skPoint(sketch, "E11.0.8.3", {"position": v(39.06, -102.36) * mm});
            skLineSegment(sketch, "E11.0.8.4", {"start": v(-66.8, -107.44) * mm, "end": v(-66.8, -119.62) * mm});
            skLineSegment(sketch, "E11.0.8.5", {"start": v(-95, -107.44) * mm, "end": v(-95, -119.62) * mm});
            skLineSegment(sketch, "E11.0.8.6", {"start": v(-73.71, -107.44) * mm, "end": v(-73.71, -119.62) * mm});
            skLineSegment(sketch, "E11.0.8.7", {"start": v(-123.2, -107.44) * mm, "end": v(-123.2, -119.62) * mm});
            skLineSegment(sketch, "E11.0.8.8", {"start": v(-101.9, -107.44) * mm, "end": v(-101.9, -119.62) * mm});
            skPoint(sketch, "E11.0.8.9", {"position": v(130.56, -124.7) * mm});
            skPoint(sketch, "E11.0.8.10", {"position": v(67.26, -102.36) * mm});
            skPoint(sketch, "E11.0.8.11", {"position": v(-66.8, -124.7) * mm});
            skPoint(sketch, "E11.0.8.12", {"position": v(10.87, -102.36) * mm});
            skPoint(sketch, "E11.0.8.13", {"position": v(-101.9, -124.7) * mm});
            skPoint(sketch, "E11.0.8.14", {"position": v(45.97, -124.7) * mm});
            skLineSegment(sketch, "E11.0.8.15", {"start": v(-118.11, -102.36) * mm, "end": v(-106.99, -102.36) * mm});
            skPoint(sketch, "E11.0.8.16", {"position": v(-45.52, -102.36) * mm});
            skPoint(sketch, "E11.0.8.17", {"position": v(151.84, -102.36) * mm});
            skPoint(sketch, "E11.0.8.18", {"position": v(123.65, -102.36) * mm});
            skLineSegment(sketch, "E11.0.8.19", {"start": v(151.84, -107.44) * mm, "end": v(151.84, -119.62) * mm});
            skLineSegment(sketch, "E11.0.8.20", {"start": v(95.45, -107.44) * mm, "end": v(95.45, -119.62) * mm});
            skLineSegment(sketch, "E11.0.8.21", {"start": v(39.06, -107.44) * mm, "end": v(39.06, -119.62) * mm});
            skLineSegment(sketch, "E11.0.8.22", {"start": v(-17.32, -107.44) * mm, "end": v(-17.32, -119.62) * mm});
            skPoint(sketch, "E11.0.8.23", {"position": v(74.17, -124.7) * mm});
            skPoint(sketch, "E11.0.8.24", {"position": v(-38.6, -124.7) * mm});
            skLineSegment(sketch, "E11.0.8.25", {"start": v(-10.41, -107.44) * mm, "end": v(-10.41, -119.62) * mm});
            skLineSegment(sketch, "E11.0.8.26", {"start": v(-89.92, -124.7) * mm, "end": v(-78.8, -124.7) * mm});
            skLineSegment(sketch, "E11.0.8.27", {"start": v(-45.52, -107.44) * mm, "end": v(-45.52, -119.62) * mm});
            skLineSegment(sketch, "E11.0.8.28", {"start": v(10.87, -107.44) * mm, "end": v(10.87, -119.62) * mm});
            skPoint(sketch, "E11.0.8.29", {"position": v(-17.32, -102.36) * mm});
            skPoint(sketch, "E11.0.8.30", {"position": v(95.45, -102.36) * mm});
            skPoint(sketch, "E11.0.8.31", {"position": v(95.45, -124.7) * mm});
            skPoint(sketch, "E11.0.8.32", {"position": v(151.84, -124.7) * mm});
            skPoint(sketch, "E11.0.8.33", {"position": v(-73.71, -124.7) * mm});
            skPoint(sketch, "E11.0.8.34", {"position": v(39.06, -124.7) * mm});
            skLineSegment(sketch, "E11.0.8.35", {"start": v(67.26, -107.44) * mm, "end": v(67.26, -119.62) * mm});
            skLineSegment(sketch, "E11.0.8.36", {"start": v(123.65, -107.44) * mm, "end": v(123.65, -119.62) * mm});
            skLineSegment(sketch, "E11.0.8.37", {"start": v(-123.2, -124.7) * mm, "end": v(-95, -124.7) * mm, "construction": true});
            skPoint(sketch, "E11.0.8.38", {"position": v(130.56, -102.36) * mm});
            skPoint(sketch, "E11.0.8.39", {"position": v(45.97, -102.36) * mm});
            skLineSegment(sketch, "E11.0.8.40", {"start": v(51.05, -102.36) * mm, "end": v(62.18, -102.36) * mm});
            skPoint(sketch, "E11.0.8.41", {"position": v(-66.8, -102.36) * mm});
            skLineSegment(sketch, "E11.0.8.42", {"start": v(107.44, -102.36) * mm, "end": v(118.57, -102.36) * mm});
            skLineSegment(sketch, "E11.0.8.43", {"start": v(135.64, -102.36) * mm, "end": v(146.76, -102.36) * mm});
            skLineSegment(sketch, "E11.0.8.44", {"start": v(79.25, -102.36) * mm, "end": v(90.37, -102.36) * mm});
            skLineSegment(sketch, "E11.0.8.45", {"start": v(22.86, -102.36) * mm, "end": v(33.98, -102.36) * mm});
            skLineSegment(sketch, "E11.0.8.46", {"start": v(-33.53, -102.36) * mm, "end": v(-22.4, -102.36) * mm});
            skLineSegment(sketch, "E11.0.8.47", {"start": v(-61.72, -102.36) * mm, "end": v(-50.6, -102.36) * mm});
            skPoint(sketch, "E11.0.8.48", {"position": v(-17.32, -124.7) * mm});
            skLineSegment(sketch, "E11.0.8.49", {"start": v(-5.33, -102.36) * mm, "end": v(5.79, -102.36) * mm});
            skLineSegment(sketch, "E11.0.8.50", {"start": v(-33.53, -124.7) * mm, "end": v(-22.4, -124.7) * mm});
            skLineSegment(sketch, "E11.0.8.51", {"start": v(22.86, -124.7) * mm, "end": v(33.98, -124.7) * mm});
            skPoint(sketch, "E11.0.8.52", {"position": v(17.78, -102.36) * mm});
            skLineSegment(sketch, "E11.0.8.53", {"start": v(79.25, -124.7) * mm, "end": v(90.37, -124.7) * mm});
            skLineSegment(sketch, "E11.0.8.54", {"start": v(135.64, -124.7) * mm, "end": v(146.76, -124.7) * mm});
            skPoint(sketch, "E11.0.8.55", {"position": v(67.26, -124.7) * mm});
            skPoint(sketch, "E11.0.8.56", {"position": v(-101.9, -102.36) * mm});
            skPoint(sketch, "E11.0.8.57", {"position": v(10.87, -124.7) * mm});
            skPoint(sketch, "E11.0.8.58", {"position": v(123.65, -124.7) * mm});
            skPoint(sketch, "E11.0.8.59", {"position": v(-45.52, -124.7) * mm});
            skPoint(sketch, "E11.0.8.60", {"position": v(-95, -124.7) * mm});
            skLineSegment(sketch, "E11.0.8.61", {"start": v(51.05, -124.7) * mm, "end": v(62.18, -124.7) * mm});
            skPoint(sketch, "E11.0.8.62", {"position": v(17.78, -124.7) * mm});
            skLineSegment(sketch, "E11.0.8.63", {"start": v(107.44, -124.7) * mm, "end": v(118.57, -124.7) * mm});
            skLineSegment(sketch, "E11.0.8.64", {"start": v(-61.72, -124.7) * mm, "end": v(-50.6, -124.7) * mm});
            skLineSegment(sketch, "E11.0.8.65", {"start": v(-5.33, -124.7) * mm, "end": v(5.79, -124.7) * mm});
            skPoint(sketch, "E11.0.8.66", {"position": v(-123.2, -102.36) * mm});
            skPoint(sketch, "E11.0.8.67", {"position": v(-10.41, -102.36) * mm});
            skPoint(sketch, "E11.0.8.68", {"position": v(102.36, -102.36) * mm});
            skPoint(sketch, "E11.0.8.69", {"position": v(74.17, -102.36) * mm});
            skPoint(sketch, "E11.0.8.70", {"position": v(-10.41, -124.7) * mm});
            skPoint(sketch, "E11.0.8.71", {"position": v(102.36, -124.7) * mm});
            skPoint(sketch, "E11.0.8.72", {"position": v(-38.6, -102.36) * mm});
            skPoint(sketch, "E11.0.8.73", {"position": v(-123.2, -124.7) * mm});
            skPoint(sketch, "E11.0.8.74", {"position": v(-95, -102.36) * mm});
            skLineSegment(sketch, "E11.0.8.75", {"start": v(-38.6, -107.44) * mm, "end": v(-38.6, -119.62) * mm});
            skLineSegment(sketch, "E11.0.8.76", {"start": v(17.78, -107.44) * mm, "end": v(17.78, -119.62) * mm});
            skLineSegment(sketch, "E11.0.8.77", {"start": v(74.17, -107.44) * mm, "end": v(74.17, -119.62) * mm});
            skLineSegment(sketch, "E11.0.8.78", {"start": v(130.56, -107.44) * mm, "end": v(130.56, -119.62) * mm});
            skLineSegment(sketch, "E11.0.8.79", {"start": v(-118.11, -124.7) * mm, "end": v(-106.99, -124.7) * mm});
            skLineSegment(sketch, "E11.0.8.80", {"start": v(-89.92, -102.36) * mm, "end": v(-78.8, -102.36) * mm});
            skLineSegment(sketch, "E11.0.8.81", {"start": v(-78.8, -102.36) * mm, "end": v(-73.71, -107.44) * mm});
            skLineSegment(sketch, "E11.0.8.82", {"start": v(-95, -119.62) * mm, "end": v(-89.92, -124.7) * mm});
            skLineSegment(sketch, "E11.0.8.83", {"start": v(33.98, -102.36) * mm, "end": v(39.06, -107.44) * mm});
            skLineSegment(sketch, "E11.0.8.84", {"start": v(-73.71, -119.62) * mm, "end": v(-78.8, -124.7) * mm});
            skLineSegment(sketch, "E11.0.8.85", {"start": v(-123.2, -107.44) * mm, "end": v(-118.11, -102.36) * mm});
            skLineSegment(sketch, "E11.0.8.86", {"start": v(-106.99, -102.36) * mm, "end": v(-101.9, -107.44) * mm});
            skLineSegment(sketch, "E11.0.8.87", {"start": v(-123.2, -119.62) * mm, "end": v(-118.11, -124.7) * mm});
            skLineSegment(sketch, "E11.0.8.88", {"start": v(-101.9, -119.62) * mm, "end": v(-106.99, -124.7) * mm});
            skLineSegment(sketch, "E11.0.8.89", {"start": v(-45.52, -119.62) * mm, "end": v(-50.6, -124.7) * mm});
            skLineSegment(sketch, "E11.0.8.90", {"start": v(10.87, -119.62) * mm, "end": v(5.79, -124.7) * mm});
            skLineSegment(sketch, "E11.0.8.91", {"start": v(67.26, -119.62) * mm, "end": v(62.18, -124.7) * mm});
            skLineSegment(sketch, "E11.0.8.92", {"start": v(123.65, -119.62) * mm, "end": v(118.57, -124.7) * mm});
            skLineSegment(sketch, "E11.0.8.93", {"start": v(62.18, -102.36) * mm, "end": v(67.26, -107.44) * mm});
            skLineSegment(sketch, "E11.0.8.94", {"start": v(39.06, -119.62) * mm, "end": v(33.98, -124.7) * mm});
            skLineSegment(sketch, "E11.0.8.95", {"start": v(118.57, -102.36) * mm, "end": v(123.65, -107.44) * mm});
            skLineSegment(sketch, "E11.0.8.96", {"start": v(95.45, -119.62) * mm, "end": v(90.37, -124.7) * mm});
            skLineSegment(sketch, "E11.0.8.97", {"start": v(151.84, -119.62) * mm, "end": v(146.76, -124.7) * mm});
            skLineSegment(sketch, "E11.0.8.98", {"start": v(-50.6, -102.36) * mm, "end": v(-45.52, -107.44) * mm});
            skLineSegment(sketch, "E11.0.8.99", {"start": v(5.79, -102.36) * mm, "end": v(10.87, -107.44) * mm});
            skLineSegment(sketch, "E11.0.8.100", {"start": v(-17.32, -119.62) * mm, "end": v(-22.4, -124.7) * mm});
            skLineSegment(sketch, "E11.0.8.101", {"start": v(-38.6, -119.62) * mm, "end": v(-33.53, -124.7) * mm});
            skLineSegment(sketch, "E11.0.8.102", {"start": v(-10.41, -107.44) * mm, "end": v(-5.33, -102.36) * mm});
            skLineSegment(sketch, "E11.0.8.103", {"start": v(-66.8, -107.44) * mm, "end": v(-61.72, -102.36) * mm});
            skLineSegment(sketch, "E11.0.8.104", {"start": v(130.56, -119.62) * mm, "end": v(135.64, -124.7) * mm});
            skLineSegment(sketch, "E11.0.8.105", {"start": v(102.36, -107.44) * mm, "end": v(107.44, -102.36) * mm});
            skLineSegment(sketch, "E11.0.8.106", {"start": v(74.17, -119.62) * mm, "end": v(79.25, -124.7) * mm});
            skLineSegment(sketch, "E11.0.8.107", {"start": v(45.97, -107.44) * mm, "end": v(51.05, -102.36) * mm});
            skLineSegment(sketch, "E11.0.8.108", {"start": v(17.78, -119.62) * mm, "end": v(22.86, -124.7) * mm});
            skLineSegment(sketch, "E11.0.8.109", {"start": v(130.56, -107.44) * mm, "end": v(135.64, -102.36) * mm});
            skLineSegment(sketch, "E11.0.8.110", {"start": v(74.17, -107.44) * mm, "end": v(79.25, -102.36) * mm});
            skLineSegment(sketch, "E11.0.8.111", {"start": v(17.78, -107.44) * mm, "end": v(22.86, -102.36) * mm});
            skLineSegment(sketch, "E11.0.8.112", {"start": v(-95, -107.44) * mm, "end": v(-89.92, -102.36) * mm});
            skLineSegment(sketch, "E11.0.8.113", {"start": v(-38.6, -107.44) * mm, "end": v(-33.53, -102.36) * mm});
            skLineSegment(sketch, "E11.0.8.114", {"start": v(-22.4, -102.36) * mm, "end": v(-17.32, -107.44) * mm});
            skLineSegment(sketch, "E11.0.8.115", {"start": v(-10.41, -119.62) * mm, "end": v(-5.33, -124.7) * mm});
            skLineSegment(sketch, "E11.0.8.116", {"start": v(-66.8, -119.62) * mm, "end": v(-61.72, -124.7) * mm});
            skLineSegment(sketch, "E11.0.8.117", {"start": v(146.76, -102.36) * mm, "end": v(151.84, -107.44) * mm});
            skLineSegment(sketch, "E11.0.8.118", {"start": v(102.36, -119.62) * mm, "end": v(107.44, -124.7) * mm});
            skLineSegment(sketch, "E11.0.8.119", {"start": v(90.37, -102.36) * mm, "end": v(95.45, -107.44) * mm});
            skLineSegment(sketch, "E11.0.8.120", {"start": v(45.97, -119.62) * mm, "end": v(51.05, -124.7) * mm});
            skPoint(sketch, "E11.0.9.0", {"position": v(-73.71, -130.56) * mm});
            skLineSegment(sketch, "E11.0.9.1", {"start": v(102.36, -135.64) * mm, "end": v(102.36, -147.81) * mm});
            skLineSegment(sketch, "E11.0.9.2", {"start": v(45.97, -135.64) * mm, "end": v(45.97, -147.81) * mm});
            skPoint(sketch, "E11.0.9.3", {"position": v(39.06, -130.56) * mm});
            skLineSegment(sketch, "E11.0.9.4", {"start": v(-66.8, -135.64) * mm, "end": v(-66.8, -147.81) * mm});
            skLineSegment(sketch, "E11.0.9.5", {"start": v(-95, -135.64) * mm, "end": v(-95, -147.81) * mm});
            skLineSegment(sketch, "E11.0.9.6", {"start": v(-73.71, -135.64) * mm, "end": v(-73.71, -147.81) * mm});
            skLineSegment(sketch, "E11.0.9.7", {"start": v(-123.2, -135.64) * mm, "end": v(-123.2, -147.81) * mm});
            skLineSegment(sketch, "E11.0.9.8", {"start": v(-101.9, -135.64) * mm, "end": v(-101.9, -147.81) * mm});
            skPoint(sketch, "E11.0.9.9", {"position": v(130.56, -152.9) * mm});
            skPoint(sketch, "E11.0.9.10", {"position": v(67.26, -130.56) * mm});
            skPoint(sketch, "E11.0.9.11", {"position": v(-66.8, -152.9) * mm});
            skPoint(sketch, "E11.0.9.12", {"position": v(10.87, -130.56) * mm});
            skPoint(sketch, "E11.0.9.13", {"position": v(-101.9, -152.9) * mm});
            skPoint(sketch, "E11.0.9.14", {"position": v(45.97, -152.9) * mm});
            skLineSegment(sketch, "E11.0.9.15", {"start": v(-118.11, -130.56) * mm, "end": v(-106.99, -130.56) * mm});
            skPoint(sketch, "E11.0.9.16", {"position": v(-45.52, -130.56) * mm});
            skPoint(sketch, "E11.0.9.17", {"position": v(151.84, -130.56) * mm});
            skPoint(sketch, "E11.0.9.18", {"position": v(123.65, -130.56) * mm});
            skLineSegment(sketch, "E11.0.9.19", {"start": v(151.84, -135.64) * mm, "end": v(151.84, -147.81) * mm});
            skLineSegment(sketch, "E11.0.9.20", {"start": v(95.45, -135.64) * mm, "end": v(95.45, -147.81) * mm});
            skLineSegment(sketch, "E11.0.9.21", {"start": v(39.06, -135.64) * mm, "end": v(39.06, -147.81) * mm});
            skLineSegment(sketch, "E11.0.9.22", {"start": v(-17.32, -135.64) * mm, "end": v(-17.32, -147.81) * mm});
            skPoint(sketch, "E11.0.9.23", {"position": v(74.17, -152.9) * mm});
            skPoint(sketch, "E11.0.9.24", {"position": v(-38.6, -152.9) * mm});
            skLineSegment(sketch, "E11.0.9.25", {"start": v(-10.41, -135.64) * mm, "end": v(-10.41, -147.81) * mm});
            skLineSegment(sketch, "E11.0.9.26", {"start": v(-89.92, -152.9) * mm, "end": v(-78.8, -152.9) * mm});
            skLineSegment(sketch, "E11.0.9.27", {"start": v(-45.52, -135.64) * mm, "end": v(-45.52, -147.81) * mm});
            skLineSegment(sketch, "E11.0.9.28", {"start": v(10.87, -135.64) * mm, "end": v(10.87, -147.81) * mm});
            skPoint(sketch, "E11.0.9.29", {"position": v(-17.32, -130.56) * mm});
            skPoint(sketch, "E11.0.9.30", {"position": v(95.45, -130.56) * mm});
            skPoint(sketch, "E11.0.9.31", {"position": v(95.45, -152.9) * mm});
            skPoint(sketch, "E11.0.9.32", {"position": v(151.84, -152.9) * mm});
            skPoint(sketch, "E11.0.9.33", {"position": v(-73.71, -152.9) * mm});
            skPoint(sketch, "E11.0.9.34", {"position": v(39.06, -152.9) * mm});
            skLineSegment(sketch, "E11.0.9.35", {"start": v(67.26, -135.64) * mm, "end": v(67.26, -147.81) * mm});
            skLineSegment(sketch, "E11.0.9.36", {"start": v(123.65, -135.64) * mm, "end": v(123.65, -147.81) * mm});
            skLineSegment(sketch, "E11.0.9.37", {"start": v(-123.2, -152.9) * mm, "end": v(-95, -152.9) * mm, "construction": true});
            skPoint(sketch, "E11.0.9.38", {"position": v(130.56, -130.56) * mm});
            skPoint(sketch, "E11.0.9.39", {"position": v(45.97, -130.56) * mm});
            skLineSegment(sketch, "E11.0.9.40", {"start": v(51.05, -130.56) * mm, "end": v(62.18, -130.56) * mm});
            skPoint(sketch, "E11.0.9.41", {"position": v(-66.8, -130.56) * mm});
            skLineSegment(sketch, "E11.0.9.42", {"start": v(107.44, -130.56) * mm, "end": v(118.57, -130.56) * mm});
            skLineSegment(sketch, "E11.0.9.43", {"start": v(135.64, -130.56) * mm, "end": v(146.76, -130.56) * mm});
            skLineSegment(sketch, "E11.0.9.44", {"start": v(79.25, -130.56) * mm, "end": v(90.37, -130.56) * mm});
            skLineSegment(sketch, "E11.0.9.45", {"start": v(22.86, -130.56) * mm, "end": v(33.98, -130.56) * mm});
            skLineSegment(sketch, "E11.0.9.46", {"start": v(-33.53, -130.56) * mm, "end": v(-22.4, -130.56) * mm});
            skLineSegment(sketch, "E11.0.9.47", {"start": v(-61.72, -130.56) * mm, "end": v(-50.6, -130.56) * mm});
            skPoint(sketch, "E11.0.9.48", {"position": v(-17.32, -152.9) * mm});
            skLineSegment(sketch, "E11.0.9.49", {"start": v(-5.33, -130.56) * mm, "end": v(5.79, -130.56) * mm});
            skLineSegment(sketch, "E11.0.9.50", {"start": v(-33.53, -152.9) * mm, "end": v(-22.4, -152.9) * mm});
            skLineSegment(sketch, "E11.0.9.51", {"start": v(22.86, -152.9) * mm, "end": v(33.98, -152.9) * mm});
            skPoint(sketch, "E11.0.9.52", {"position": v(17.78, -130.56) * mm});
            skLineSegment(sketch, "E11.0.9.53", {"start": v(79.25, -152.9) * mm, "end": v(90.37, -152.9) * mm});
            skLineSegment(sketch, "E11.0.9.54", {"start": v(135.64, -152.9) * mm, "end": v(146.76, -152.9) * mm});
            skPoint(sketch, "E11.0.9.55", {"position": v(67.26, -152.9) * mm});
            skPoint(sketch, "E11.0.9.56", {"position": v(-101.9, -130.56) * mm});
            skPoint(sketch, "E11.0.9.57", {"position": v(10.87, -152.9) * mm});
            skPoint(sketch, "E11.0.9.58", {"position": v(123.65, -152.9) * mm});
            skPoint(sketch, "E11.0.9.59", {"position": v(-45.52, -152.9) * mm});
            skPoint(sketch, "E11.0.9.60", {"position": v(-95, -152.9) * mm});
            skLineSegment(sketch, "E11.0.9.61", {"start": v(51.05, -152.9) * mm, "end": v(62.18, -152.9) * mm});
            skPoint(sketch, "E11.0.9.62", {"position": v(17.78, -152.9) * mm});
            skLineSegment(sketch, "E11.0.9.63", {"start": v(107.44, -152.9) * mm, "end": v(118.57, -152.9) * mm});
            skLineSegment(sketch, "E11.0.9.64", {"start": v(-61.72, -152.9) * mm, "end": v(-50.6, -152.9) * mm});
            skLineSegment(sketch, "E11.0.9.65", {"start": v(-5.33, -152.9) * mm, "end": v(5.79, -152.9) * mm});
            skPoint(sketch, "E11.0.9.66", {"position": v(-123.2, -130.56) * mm});
            skPoint(sketch, "E11.0.9.67", {"position": v(-10.41, -130.56) * mm});
            skPoint(sketch, "E11.0.9.68", {"position": v(102.36, -130.56) * mm});
            skPoint(sketch, "E11.0.9.69", {"position": v(74.17, -130.56) * mm});
            skPoint(sketch, "E11.0.9.70", {"position": v(-10.41, -152.9) * mm});
            skPoint(sketch, "E11.0.9.71", {"position": v(102.36, -152.9) * mm});
            skPoint(sketch, "E11.0.9.72", {"position": v(-38.6, -130.56) * mm});
            skPoint(sketch, "E11.0.9.73", {"position": v(-123.2, -152.9) * mm});
            skPoint(sketch, "E11.0.9.74", {"position": v(-95, -130.56) * mm});
            skLineSegment(sketch, "E11.0.9.75", {"start": v(-38.6, -135.64) * mm, "end": v(-38.6, -147.81) * mm});
            skLineSegment(sketch, "E11.0.9.76", {"start": v(17.78, -135.64) * mm, "end": v(17.78, -147.81) * mm});
            skLineSegment(sketch, "E11.0.9.77", {"start": v(74.17, -135.64) * mm, "end": v(74.17, -147.81) * mm});
            skLineSegment(sketch, "E11.0.9.78", {"start": v(130.56, -135.64) * mm, "end": v(130.56, -147.81) * mm});
            skLineSegment(sketch, "E11.0.9.79", {"start": v(-118.11, -152.9) * mm, "end": v(-106.99, -152.9) * mm});
            skLineSegment(sketch, "E11.0.9.80", {"start": v(-89.92, -130.56) * mm, "end": v(-78.8, -130.56) * mm});
            skLineSegment(sketch, "E11.0.9.81", {"start": v(-78.8, -130.56) * mm, "end": v(-73.71, -135.64) * mm});
            skLineSegment(sketch, "E11.0.9.82", {"start": v(-95, -147.81) * mm, "end": v(-89.92, -152.9) * mm});
            skLineSegment(sketch, "E11.0.9.83", {"start": v(33.98, -130.56) * mm, "end": v(39.06, -135.64) * mm});
            skLineSegment(sketch, "E11.0.9.84", {"start": v(-73.71, -147.81) * mm, "end": v(-78.8, -152.9) * mm});
            skLineSegment(sketch, "E11.0.9.85", {"start": v(-123.2, -135.64) * mm, "end": v(-118.11, -130.56) * mm});
            skLineSegment(sketch, "E11.0.9.86", {"start": v(-106.99, -130.56) * mm, "end": v(-101.9, -135.64) * mm});
            skLineSegment(sketch, "E11.0.9.87", {"start": v(-123.19, -147.81) * mm, "end": v(-118.11, -152.9) * mm});
            skLineSegment(sketch, "E11.0.9.88", {"start": v(-101.9, -147.81) * mm, "end": v(-106.99, -152.9) * mm});
            skLineSegment(sketch, "E11.0.9.89", {"start": v(-45.52, -147.81) * mm, "end": v(-50.6, -152.9) * mm});
            skLineSegment(sketch, "E11.0.9.90", {"start": v(10.87, -147.81) * mm, "end": v(5.79, -152.9) * mm});
            skLineSegment(sketch, "E11.0.9.91", {"start": v(67.26, -147.81) * mm, "end": v(62.18, -152.9) * mm});
            skLineSegment(sketch, "E11.0.9.92", {"start": v(123.65, -147.81) * mm, "end": v(118.57, -152.9) * mm});
            skLineSegment(sketch, "E11.0.9.93", {"start": v(62.18, -130.56) * mm, "end": v(67.26, -135.64) * mm});
            skLineSegment(sketch, "E11.0.9.94", {"start": v(39.06, -147.81) * mm, "end": v(33.98, -152.9) * mm});
            skLineSegment(sketch, "E11.0.9.95", {"start": v(118.57, -130.56) * mm, "end": v(123.65, -135.64) * mm});
            skLineSegment(sketch, "E11.0.9.96", {"start": v(95.45, -147.81) * mm, "end": v(90.37, -152.9) * mm});
            skLineSegment(sketch, "E11.0.9.97", {"start": v(151.84, -147.81) * mm, "end": v(146.76, -152.9) * mm});
            skLineSegment(sketch, "E11.0.9.98", {"start": v(-50.6, -130.56) * mm, "end": v(-45.52, -135.64) * mm});
            skLineSegment(sketch, "E11.0.9.99", {"start": v(5.79, -130.56) * mm, "end": v(10.87, -135.64) * mm});
            skLineSegment(sketch, "E11.0.9.100", {"start": v(-17.32, -147.81) * mm, "end": v(-22.4, -152.9) * mm});
            skLineSegment(sketch, "E11.0.9.101", {"start": v(-38.6, -147.81) * mm, "end": v(-33.53, -152.9) * mm});
            skLineSegment(sketch, "E11.0.9.102", {"start": v(-10.41, -135.64) * mm, "end": v(-5.33, -130.56) * mm});
            skLineSegment(sketch, "E11.0.9.103", {"start": v(-66.8, -135.64) * mm, "end": v(-61.72, -130.56) * mm});
            skLineSegment(sketch, "E11.0.9.104", {"start": v(130.56, -147.81) * mm, "end": v(135.64, -152.9) * mm});
            skLineSegment(sketch, "E11.0.9.105", {"start": v(102.36, -135.64) * mm, "end": v(107.44, -130.56) * mm});
            skLineSegment(sketch, "E11.0.9.106", {"start": v(74.17, -147.81) * mm, "end": v(79.25, -152.9) * mm});
            skLineSegment(sketch, "E11.0.9.107", {"start": v(45.97, -135.64) * mm, "end": v(51.05, -130.56) * mm});
            skLineSegment(sketch, "E11.0.9.108", {"start": v(17.78, -147.81) * mm, "end": v(22.86, -152.9) * mm});
            skLineSegment(sketch, "E11.0.9.109", {"start": v(130.56, -135.64) * mm, "end": v(135.64, -130.56) * mm});
            skLineSegment(sketch, "E11.0.9.110", {"start": v(74.17, -135.64) * mm, "end": v(79.25, -130.56) * mm});
            skLineSegment(sketch, "E11.0.9.111", {"start": v(17.78, -135.64) * mm, "end": v(22.86, -130.56) * mm});
            skLineSegment(sketch, "E11.0.9.112", {"start": v(-95, -135.64) * mm, "end": v(-89.92, -130.56) * mm});
            skLineSegment(sketch, "E11.0.9.113", {"start": v(-38.6, -135.64) * mm, "end": v(-33.53, -130.56) * mm});
            skLineSegment(sketch, "E11.0.9.114", {"start": v(-22.4, -130.56) * mm, "end": v(-17.32, -135.64) * mm});
            skLineSegment(sketch, "E11.0.9.115", {"start": v(-10.41, -147.81) * mm, "end": v(-5.33, -152.9) * mm});
            skLineSegment(sketch, "E11.0.9.116", {"start": v(-66.8, -147.81) * mm, "end": v(-61.72, -152.9) * mm});
            skLineSegment(sketch, "E11.0.9.117", {"start": v(146.76, -130.56) * mm, "end": v(151.84, -135.64) * mm});
            skLineSegment(sketch, "E11.0.9.118", {"start": v(102.36, -147.81) * mm, "end": v(107.44, -152.9) * mm});
            skLineSegment(sketch, "E11.0.9.119", {"start": v(90.37, -130.56) * mm, "end": v(95.45, -135.64) * mm});
            skLineSegment(sketch, "E11.0.9.120", {"start": v(45.97, -147.81) * mm, "end": v(51.05, -152.9) * mm});
            skLineSegment(sketch, "E11.direction1", {"start": v(-123.2, 100.85) * mm, "end": v(-97.8, 100.85) * mm, "construction": true});
            skLineSegment(sketch, "E11.direction2", {"start": v(-123.2, 100.85) * mm, "end": v(-123.2, 72.66) * mm, "construction": true});
            skSolve(sketch);
        }
        {
            var Q0;
            Q0 = qSketchRegion(id + "F2", true);
            extrude(context, id + "F3", {"entities" : qUnion([Q0]), "operationType" : NewBodyOperationType.REMOVE, "oppositeDirection" : true, "depth" : 25.4 * mm, "offsetDistance" : 25.4 * mm});
        }
    });
